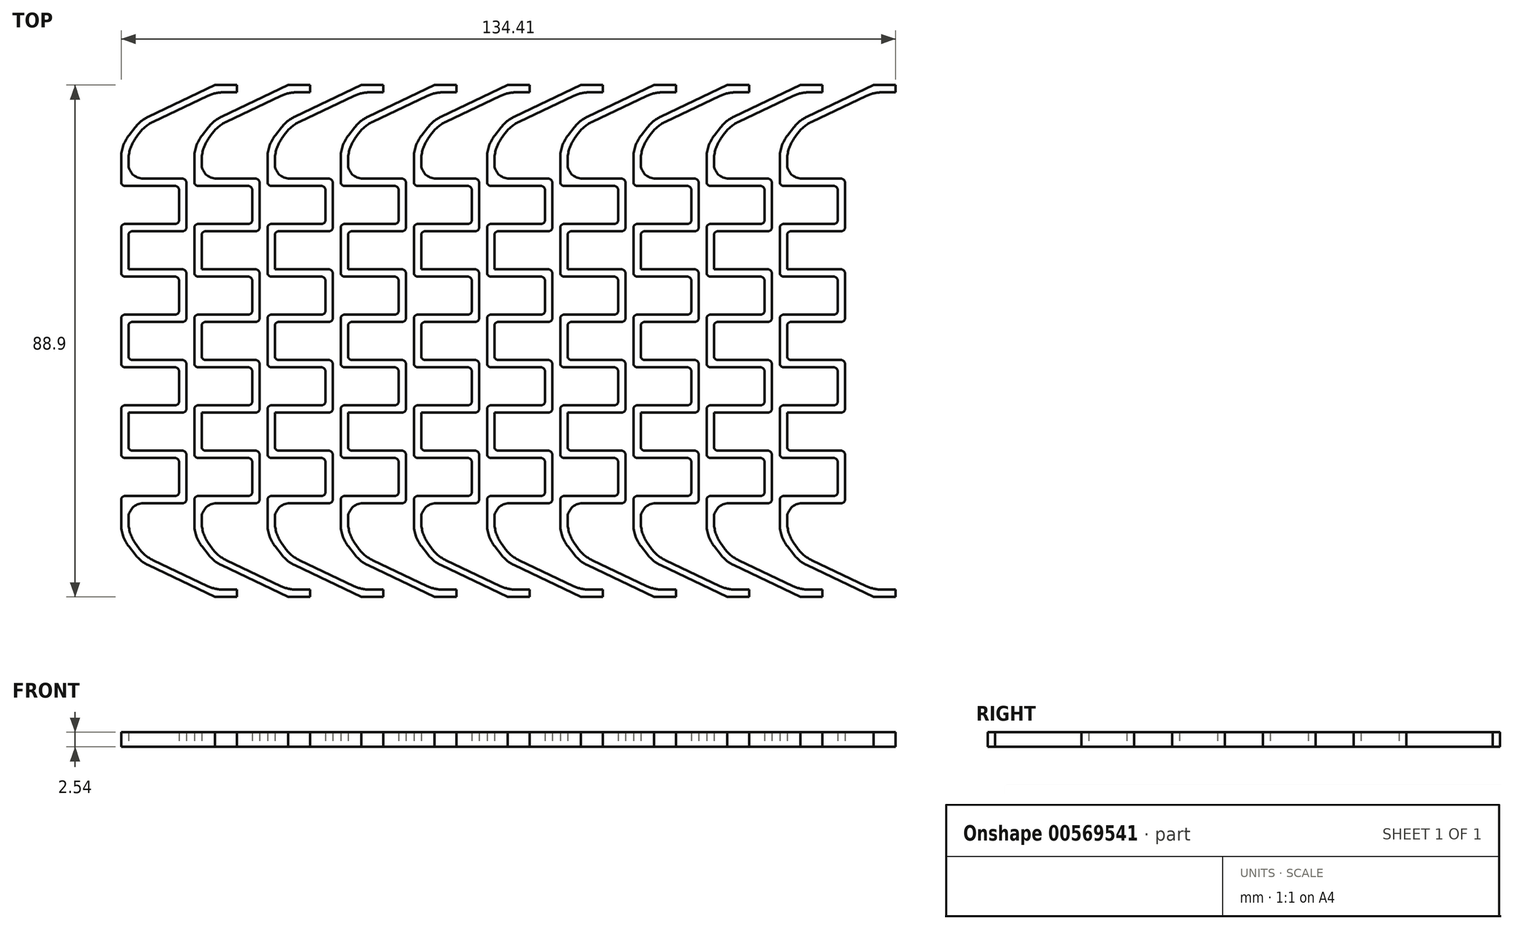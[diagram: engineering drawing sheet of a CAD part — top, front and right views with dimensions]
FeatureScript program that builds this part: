
annotation { "Feature Type Name" : "Feature", "Feature Type Description" : "" }
export const myFeature = defineFeature(function(context is Context, id is Id, definition is map)
    precondition{}
    {
        {
            var Q0;
            Q0=qCreatedBy(makeId("Top.planeOp"),FACE);
            var sketch = newSketch(context, id + "F0", { "sketchPlane" : qUnion([Q0])});
            skLineSegment(sketch, "E0", {"start": v(0, 44.45) * mm, "end": v(-11.59, 38.94) * mm});
            skLineSegment(sketch, "E1", {"start": v(0, 44.45) * mm, "end": v(3.81, 44.45) * mm});
            skLineSegment(sketch, "E2", {"start": v(3.81, 44.45) * mm, "end": v(3.81, 43.18) * mm});
            skLineSegment(sketch, "E3", {"start": v(3.81, 43.18) * mm, "end": v(1.43, 43.18) * mm});
            skPoint(sketch, "E4.visualSharp", {"position": v(0, 43.18) * mm});
            skLineSegment(sketch, "E5", {"start": v(-1.3, 42.56) * mm, "end": v(-10.77, 38.06) * mm});
            skLineSegment(sketch, "E6", {"start": v(-13.88, 37.1) * mm, "end": v(-14.96, 35.7) * mm});
            skLineSegment(sketch, "E7", {"start": v(-16.3, 31.8) * mm, "end": v(-16.3, 27.6) * mm});
            skLineSegment(sketch, "E8", {"start": v(-15.63, 26.92) * mm, "end": v(-6.93, 26.92) * mm});
            skLineSegment(sketch, "E9", {"start": v(-6.25, 26.25) * mm, "end": v(-6.25, 21) * mm});
            skLineSegment(sketch, "E10", {"start": v(-6.93, 20.32) * mm, "end": v(-15.63, 20.32) * mm});
            skLineSegment(sketch, "E11", {"start": v(-16.3, 19.65) * mm, "end": v(-16.3, 11.85) * mm});
            skLineSegment(sketch, "E12", {"start": v(-15.63, 11.18) * mm, "end": v(-6.93, 11.18) * mm});
            skLineSegment(sketch, "E13", {"start": v(-6.25, 10.5) * mm, "end": v(-6.25, 5.24) * mm});
            skLineSegment(sketch, "E14", {"start": v(-6.93, 4.57) * mm, "end": v(-15.63, 4.57) * mm});
            skLineSegment(sketch, "E15", {"start": v(-16.3, 3.9) * mm, "end": v(-16.3, 0) * mm});
            skLineSegment(sketch, "E16", {"start": v(-13.22, 36) * mm, "end": v(-13.85, 35.1) * mm});
            skLineSegment(sketch, "E17", {"start": v(-15.03, 31.43) * mm, "end": v(-15.03, 30.73) * mm});
            skLineSegment(sketch, "E18", {"start": v(-12.49, 28.2) * mm, "end": v(-5.66, 28.2) * mm});
            skLineSegment(sketch, "E19", {"start": v(-4.98, 27.52) * mm, "end": v(-4.98, 19.72) * mm});
            skLineSegment(sketch, "E20", {"start": v(-5.66, 19.05) * mm, "end": v(-14.36, 19.05) * mm});
            skLineSegment(sketch, "E21", {"start": v(-15.03, 18.38) * mm, "end": v(-15.03, 12.45) * mm});
            skLineSegment(sketch, "E22", {"start": v(-15.03, 12.45) * mm, "end": v(-5.66, 12.45) * mm});
            skLineSegment(sketch, "E23", {"start": v(-4.98, 11.77) * mm, "end": v(-4.98, 3.97) * mm});
            skLineSegment(sketch, "E24", {"start": v(-5.66, 3.3) * mm, "end": v(-14.36, 3.3) * mm});
            skLineSegment(sketch, "E25", {"start": v(-15.03, 2.63) * mm, "end": v(-15.03, 0) * mm});
            skArc(sketch, "E26.filletArc", {"start": v(1.43, 43.18) * mm, "mid": v(0.04, 43.02) * mm, "end": v(-1.3, 42.56) * mm});
            skPoint(sketch, "E27.visualSharp", {"position": v(-12.26, 37.35) * mm});
            skArc(sketch, "E27.filletArc", {"start": v(-10.77, 38.06) * mm, "mid": v(-12.13, 37.19) * mm, "end": v(-13.22, 36) * mm});
            skPoint(sketch, "E28.visualSharp", {"position": v(-15.03, 33.45) * mm});
            skArc(sketch, "E28.filletArc", {"start": v(-13.85, 35.1) * mm, "mid": v(-14.73, 33.36) * mm, "end": v(-15.03, 31.43) * mm});
            skPoint(sketch, "E29.visualSharp", {"position": v(-16.3, 33.98) * mm});
            skArc(sketch, "E29.filletArc", {"start": v(-14.96, 35.7) * mm, "mid": v(-15.96, 33.86) * mm, "end": v(-16.3, 31.8) * mm});
            skPoint(sketch, "E30.visualSharp", {"position": v(-12.95, 38.29) * mm});
            skArc(sketch, "E30.filletArc", {"start": v(-11.59, 38.94) * mm, "mid": v(-12.84, 38.15) * mm, "end": v(-13.88, 37.1) * mm});
            skPoint(sketch, "E31.visualSharp", {"position": v(-15.03, 28.2) * mm});
            skArc(sketch, "E31.filletArc", {"start": v(-15.03, 30.73) * mm, "mid": v(-14.29, 28.94) * mm, "end": v(-12.49, 28.2) * mm});
            skPoint(sketch, "E32.visualSharp", {"position": v(-16.3, 26.92) * mm});
            skArc(sketch, "E32.filletArc", {"start": v(-16.3, 27.6) * mm, "mid": v(-16.1, 27.12) * mm, "end": v(-15.63, 26.92) * mm});
            skPoint(sketch, "E33.visualSharp", {"position": v(-6.25, 26.92) * mm});
            skArc(sketch, "E33.filletArc", {"start": v(-6.25, 26.25) * mm, "mid": v(-6.45, 26.73) * mm, "end": v(-6.93, 26.92) * mm});
            skPoint(sketch, "E34.visualSharp", {"position": v(-4.98, 28.2) * mm});
            skArc(sketch, "E34.filletArc", {"start": v(-4.98, 27.52) * mm, "mid": v(-5.18, 28) * mm, "end": v(-5.66, 28.2) * mm});
            skPoint(sketch, "E35.visualSharp", {"position": v(-6.25, 20.32) * mm});
            skArc(sketch, "E35.filletArc", {"start": v(-6.93, 20.32) * mm, "mid": v(-6.45, 20.52) * mm, "end": v(-6.25, 21) * mm});
            skPoint(sketch, "E36.visualSharp", {"position": v(-4.98, 19.05) * mm});
            skArc(sketch, "E36.filletArc", {"start": v(-5.66, 19.05) * mm, "mid": v(-5.18, 19.25) * mm, "end": v(-4.98, 19.72) * mm});
            skPoint(sketch, "E37.visualSharp", {"position": v(-16.3, 20.32) * mm});
            skArc(sketch, "E37.filletArc", {"start": v(-15.63, 20.32) * mm, "mid": v(-16.1, 20.12) * mm, "end": v(-16.3, 19.65) * mm});
            skPoint(sketch, "E38.visualSharp", {"position": v(-16.3, 11.18) * mm});
            skArc(sketch, "E38.filletArc", {"start": v(-16.3, 11.85) * mm, "mid": v(-16.1, 11.37) * mm, "end": v(-15.63, 11.18) * mm});
            skPoint(sketch, "E39.visualSharp", {"position": v(-15.03, 19.05) * mm});
            skArc(sketch, "E39.filletArc", {"start": v(-14.36, 19.05) * mm, "mid": v(-14.83, 18.85) * mm, "end": v(-15.03, 18.38) * mm});
            skPoint(sketch, "E40.visualSharp", {"position": v(-4.98, 12.45) * mm});
            skArc(sketch, "E40.filletArc", {"start": v(-4.98, 11.77) * mm, "mid": v(-5.18, 12.25) * mm, "end": v(-5.66, 12.45) * mm});
            skPoint(sketch, "E41.visualSharp", {"position": v(-6.25, 11.18) * mm});
            skArc(sketch, "E41.filletArc", {"start": v(-6.25, 10.5) * mm, "mid": v(-6.45, 10.98) * mm, "end": v(-6.93, 11.18) * mm});
            skPoint(sketch, "E42.visualSharp", {"position": v(-4.98, 3.3) * mm});
            skArc(sketch, "E42.filletArc", {"start": v(-5.66, 3.3) * mm, "mid": v(-5.18, 3.5) * mm, "end": v(-4.98, 3.97) * mm});
            skPoint(sketch, "E43.visualSharp", {"position": v(-15.03, 3.3) * mm});
            skArc(sketch, "E43.filletArc", {"start": v(-14.36, 3.3) * mm, "mid": v(-14.83, 3.1) * mm, "end": v(-15.03, 2.63) * mm});
            skPoint(sketch, "E44.visualSharp", {"position": v(-6.25, 4.57) * mm});
            skArc(sketch, "E44.filletArc", {"start": v(-6.93, 4.57) * mm, "mid": v(-6.45, 4.77) * mm, "end": v(-6.25, 5.24) * mm});
            skPoint(sketch, "E45.visualSharp", {"position": v(-16.3, 4.57) * mm});
            skArc(sketch, "E45.filletArc", {"start": v(-15.63, 4.57) * mm, "mid": v(-16.1, 4.38) * mm, "end": v(-16.3, 3.9) * mm});
            skArc(sketch, "E46.MirrorCS", {"start": v(-15.03, -30.73) * mm, "mid": v(-14.29, -28.94) * mm, "end": v(-12.49, -28.2) * mm});
            skArc(sketch, "E47.MirrorCS", {"start": v(-15.63, -4.57) * mm, "mid": v(-16.1, -4.38) * mm, "end": v(-16.3, -3.9) * mm});
            skArc(sketch, "E48.MirrorCS", {"start": v(-14.36, -19.05) * mm, "mid": v(-14.83, -18.85) * mm, "end": v(-15.03, -18.38) * mm});
            skArc(sketch, "E49.MirrorCS", {"start": v(-14.36, -3.3) * mm, "mid": v(-14.83, -3.1) * mm, "end": v(-15.03, -2.63) * mm});
            skArc(sketch, "E50.MirrorCS", {"start": v(-6.25, -26.25) * mm, "mid": v(-6.45, -26.73) * mm, "end": v(-6.93, -26.92) * mm});
            skArc(sketch, "E51.MirrorCS", {"start": v(-4.98, -27.52) * mm, "mid": v(-5.18, -28) * mm, "end": v(-5.66, -28.2) * mm});
            skArc(sketch, "E52.MirrorCS", {"start": v(-15.63, -20.32) * mm, "mid": v(-16.1, -20.12) * mm, "end": v(-16.3, -19.65) * mm});
            skArc(sketch, "E53.MirrorCS", {"start": v(-6.25, -10.5) * mm, "mid": v(-6.45, -10.98) * mm, "end": v(-6.93, -11.18) * mm});
            skArc(sketch, "E54.MirrorCS", {"start": v(-6.93, -20.32) * mm, "mid": v(-6.45, -20.52) * mm, "end": v(-6.25, -21) * mm});
            skArc(sketch, "E55.MirrorCS", {"start": v(-5.66, -19.05) * mm, "mid": v(-5.18, -19.25) * mm, "end": v(-4.98, -19.72) * mm});
            skArc(sketch, "E56.MirrorCS", {"start": v(-16.3, -11.85) * mm, "mid": v(-16.1, -11.37) * mm, "end": v(-15.63, -11.18) * mm});
            skArc(sketch, "E57.MirrorCS", {"start": v(-4.98, -11.77) * mm, "mid": v(-5.18, -12.25) * mm, "end": v(-5.66, -12.45) * mm});
            skLineSegment(sketch, "E58.MirrorCS", {"start": v(-13.22, -36) * mm, "end": v(-13.85, -35.1) * mm});
            skArc(sketch, "E59.MirrorCS", {"start": v(-6.93, -4.57) * mm, "mid": v(-6.45, -4.77) * mm, "end": v(-6.25, -5.24) * mm});
            skArc(sketch, "E60.MirrorCS", {"start": v(-5.66, -3.3) * mm, "mid": v(-5.18, -3.5) * mm, "end": v(-4.98, -3.97) * mm});
            skArc(sketch, "E61.MirrorCS", {"start": v(-16.3, -27.6) * mm, "mid": v(-16.1, -27.12) * mm, "end": v(-15.63, -26.92) * mm});
            skArc(sketch, "E62.MirrorCS", {"start": v(-11.59, -38.94) * mm, "mid": v(-12.84, -38.15) * mm, "end": v(-13.88, -37.1) * mm});
            skLineSegment(sketch, "E63.MirrorCS", {"start": v(-15.03, -31.43) * mm, "end": v(-15.03, -30.73) * mm});
            skLineSegment(sketch, "E64.MirrorCS", {"start": v(-13.88, -37.1) * mm, "end": v(-14.96, -35.7) * mm});
            skLineSegment(sketch, "E65.MirrorCS", {"start": v(-16.3, -31.8) * mm, "end": v(-16.3, -27.6) * mm});
            skArc(sketch, "E66.MirrorCS", {"start": v(-10.77, -38.06) * mm, "mid": v(-12.13, -37.19) * mm, "end": v(-13.22, -36) * mm});
            skPoint(sketch, "E67.MirrorP", {"position": v(-15.03, -19.05) * mm});
            skLineSegment(sketch, "E68.MirrorCS", {"start": v(-15.03, -2.63) * mm, "end": v(-15.03, 0) * mm});
            skPoint(sketch, "E69.MirrorP", {"position": v(-15.03, -28.2) * mm});
            skArc(sketch, "E70.MirrorCS", {"start": v(-14.96, -35.7) * mm, "mid": v(-15.96, -33.86) * mm, "end": v(-16.3, -31.8) * mm});
            skArc(sketch, "E71.MirrorCS", {"start": v(-13.85, -35.1) * mm, "mid": v(-14.73, -33.36) * mm, "end": v(-15.03, -31.43) * mm});
            skPoint(sketch, "E72.MirrorP", {"position": v(-15.03, -3.3) * mm});
            skLineSegment(sketch, "E73.MirrorCS", {"start": v(-16.3, -3.9) * mm, "end": v(-16.3, 0) * mm});
            skLineSegment(sketch, "E74.MirrorCS", {"start": v(-16.3, -19.65) * mm, "end": v(-16.3, -11.85) * mm});
            skLineSegment(sketch, "E75.MirrorCS", {"start": v(-12.49, -28.2) * mm, "end": v(-5.66, -28.2) * mm});
            skPoint(sketch, "E76.MirrorP", {"position": v(-16.3, -26.92) * mm});
            skPoint(sketch, "E77.MirrorP", {"position": v(-16.3, -11.18) * mm});
            skPoint(sketch, "E78.MirrorP", {"position": v(-6.25, -20.32) * mm});
            skPoint(sketch, "E79.MirrorP", {"position": v(-4.98, -12.45) * mm});
            skLineSegment(sketch, "E80.MirrorCS", {"start": v(-15.63, -26.92) * mm, "end": v(-6.93, -26.92) * mm});
            skLineSegment(sketch, "E81.MirrorCS", {"start": v(-15.03, -18.38) * mm, "end": v(-15.03, -12.45) * mm});
            skPoint(sketch, "E82.MirrorP", {"position": v(-6.25, -11.18) * mm});
            skLineSegment(sketch, "E83.MirrorCS", {"start": v(-15.03, -12.45) * mm, "end": v(-5.66, -12.45) * mm});
            skLineSegment(sketch, "E84.MirrorCS", {"start": v(-5.66, -3.3) * mm, "end": v(-14.36, -3.3) * mm});
            skPoint(sketch, "E85.MirrorP", {"position": v(-15.03, -33.45) * mm});
            skPoint(sketch, "E86.MirrorP", {"position": v(-4.98, -3.3) * mm});
            skLineSegment(sketch, "E87.MirrorCS", {"start": v(-15.63, -11.18) * mm, "end": v(-6.93, -11.18) * mm});
            skLineSegment(sketch, "E88.MirrorCS", {"start": v(-6.25, -10.5) * mm, "end": v(-6.25, -5.24) * mm});
            skLineSegment(sketch, "E89.MirrorCS", {"start": v(-6.25, -26.25) * mm, "end": v(-6.25, -21) * mm});
            skPoint(sketch, "E90.MirrorP", {"position": v(-16.3, -33.98) * mm});
            skPoint(sketch, "E91.MirrorP", {"position": v(-16.3, -20.32) * mm});
            skPoint(sketch, "E92.MirrorP", {"position": v(-16.3, -4.57) * mm});
            skLineSegment(sketch, "E93.MirrorCS", {"start": v(-6.93, -4.57) * mm, "end": v(-15.63, -4.57) * mm});
            skPoint(sketch, "E94.MirrorP", {"position": v(-12.26, -37.35) * mm});
            skPoint(sketch, "E95.MirrorP", {"position": v(-4.98, -19.05) * mm});
            skPoint(sketch, "E96.MirrorP", {"position": v(-6.25, -4.57) * mm});
            skPoint(sketch, "E97.MirrorP", {"position": v(-4.98, -28.2) * mm});
            skLineSegment(sketch, "E98.MirrorCS", {"start": v(-5.66, -19.05) * mm, "end": v(-14.36, -19.05) * mm});
            skLineSegment(sketch, "E99.MirrorCS", {"start": v(-4.98, -11.77) * mm, "end": v(-4.98, -3.97) * mm});
            skPoint(sketch, "E100.MirrorP", {"position": v(-12.95, -38.29) * mm});
            skPoint(sketch, "E101.MirrorP", {"position": v(-6.25, -26.92) * mm});
            skLineSegment(sketch, "E102.MirrorCS", {"start": v(-4.98, -27.52) * mm, "end": v(-4.98, -19.72) * mm});
            skLineSegment(sketch, "E103.MirrorCS", {"start": v(-6.93, -20.32) * mm, "end": v(-15.63, -20.32) * mm});
            skLineSegment(sketch, "E104.MirrorCS", {"start": v(3.81, -44.45) * mm, "end": v(3.81, -43.18) * mm});
            skArc(sketch, "E105.MirrorCS", {"start": v(1.43, -43.18) * mm, "mid": v(0.04, -43.02) * mm, "end": v(-1.3, -42.56) * mm});
            skPoint(sketch, "E106.MirrorP", {"position": v(0, -43.18) * mm});
            skLineSegment(sketch, "E107.MirrorCS", {"start": v(3.81, -43.18) * mm, "end": v(1.43, -43.18) * mm});
            skLineSegment(sketch, "E108.MirrorCS", {"start": v(0, -44.45) * mm, "end": v(3.81, -44.45) * mm});
            skLineSegment(sketch, "E109.MirrorCS", {"start": v(-1.3, -42.56) * mm, "end": v(-10.77, -38.06) * mm});
            skLineSegment(sketch, "E110.MirrorCS", {"start": v(0, -44.45) * mm, "end": v(-11.59, -38.94) * mm});
            skPoint(sketch, "E111.1.0.0", {"position": v(-2.33, 33.45) * mm});
            skPoint(sketch, "E111.1.0.1", {"position": v(7.72, 19.05) * mm});
            skPoint(sketch, "E111.1.0.2", {"position": v(-3.6, -26.92) * mm});
            skLineSegment(sketch, "E111.1.0.3", {"start": v(-2.33, -12.45) * mm, "end": v(7.04, -12.45) * mm});
            skLineSegment(sketch, "E111.1.0.4", {"start": v(5.77, -20.32) * mm, "end": v(-2.93, -20.32) * mm});
            skPoint(sketch, "E111.1.0.5", {"position": v(-3.6, -33.98) * mm});
            skPoint(sketch, "E111.1.0.6", {"position": v(-0.25, 38.29) * mm});
            skPoint(sketch, "E111.1.0.7", {"position": v(0.44, -37.35) * mm});
            skPoint(sketch, "E111.1.0.8", {"position": v(-3.6, -11.18) * mm});
            skLineSegment(sketch, "E111.1.0.9", {"start": v(7.04, -3.3) * mm, "end": v(-1.66, -3.3) * mm});
            skPoint(sketch, "E111.1.0.10", {"position": v(-3.6, 20.32) * mm});
            skPoint(sketch, "E111.1.0.11", {"position": v(-3.6, -20.32) * mm});
            skPoint(sketch, "E111.1.0.12", {"position": v(-3.6, 33.98) * mm});
            skPoint(sketch, "E111.1.0.13", {"position": v(7.72, -3.3) * mm});
            skPoint(sketch, "E111.1.0.14", {"position": v(6.45, -11.18) * mm});
            skPoint(sketch, "E111.1.0.15", {"position": v(7.72, -12.45) * mm});
            skLineSegment(sketch, "E111.1.0.16", {"start": v(5.77, -4.57) * mm, "end": v(-2.93, -4.57) * mm});
            skPoint(sketch, "E111.1.0.17", {"position": v(12.7, -43.18) * mm});
            skPoint(sketch, "E111.1.0.18", {"position": v(7.72, -19.05) * mm});
            skPoint(sketch, "E111.1.0.19", {"position": v(12.7, 43.18) * mm});
            skPoint(sketch, "E111.1.0.20", {"position": v(7.72, -28.2) * mm});
            skPoint(sketch, "E111.1.0.21", {"position": v(-3.6, 26.92) * mm});
            skPoint(sketch, "E111.1.0.22", {"position": v(0.44, 37.35) * mm});
            skPoint(sketch, "E111.1.0.23", {"position": v(-2.33, -33.45) * mm});
            skLineSegment(sketch, "E111.1.0.24", {"start": v(12.7, 44.45) * mm, "end": v(1.11, 38.94) * mm});
            skPoint(sketch, "E111.1.0.25", {"position": v(6.45, -20.32) * mm});
            skPoint(sketch, "E111.1.0.26", {"position": v(-2.33, -3.3) * mm});
            skPoint(sketch, "E111.1.0.27", {"position": v(6.45, -26.92) * mm});
            skLineSegment(sketch, "E111.1.0.28", {"start": v(7.04, -19.05) * mm, "end": v(-1.66, -19.05) * mm});
            skLineSegment(sketch, "E111.1.0.29", {"start": v(11.4, -42.56) * mm, "end": v(1.93, -38.06) * mm});
            skPoint(sketch, "E111.1.0.30", {"position": v(-3.6, -4.57) * mm});
            skPoint(sketch, "E111.1.0.31", {"position": v(-2.33, -28.2) * mm});
            skLineSegment(sketch, "E111.1.0.32", {"start": v(12.7, -44.45) * mm, "end": v(1.11, -38.94) * mm});
            skLineSegment(sketch, "E111.1.0.33", {"start": v(11.4, 42.56) * mm, "end": v(1.93, 38.06) * mm});
            skPoint(sketch, "E111.1.0.34", {"position": v(6.45, -4.57) * mm});
            skPoint(sketch, "E111.1.0.35", {"position": v(-0.25, -38.29) * mm});
            skLineSegment(sketch, "E111.1.0.36", {"start": v(-2.93, -11.18) * mm, "end": v(5.77, -11.18) * mm});
            skPoint(sketch, "E111.1.0.37", {"position": v(-2.33, -19.05) * mm});
            skPoint(sketch, "E111.1.0.38", {"position": v(6.45, 4.57) * mm});
            skPoint(sketch, "E111.1.0.39", {"position": v(6.45, 26.92) * mm});
            skPoint(sketch, "E111.1.0.40", {"position": v(6.45, 11.18) * mm});
            skLineSegment(sketch, "E111.1.0.41", {"start": v(7.04, 19.05) * mm, "end": v(-1.66, 19.05) * mm});
            skPoint(sketch, "E111.1.0.42", {"position": v(12.7, 43.18) * mm});
            skPoint(sketch, "E111.1.0.43", {"position": v(12.7, -43.18) * mm});
            skPoint(sketch, "E111.1.0.44", {"position": v(-3.6, 11.18) * mm});
            skPoint(sketch, "E111.1.0.45", {"position": v(-3.6, 4.57) * mm});
            skLineSegment(sketch, "E111.1.0.46", {"start": v(7.04, 3.3) * mm, "end": v(-1.66, 3.3) * mm});
            skLineSegment(sketch, "E111.1.0.47", {"start": v(5.77, 4.57) * mm, "end": v(-2.93, 4.57) * mm});
            skPoint(sketch, "E111.1.0.48", {"position": v(6.45, 20.32) * mm});
            skPoint(sketch, "E111.1.0.49", {"position": v(-2.33, 19.05) * mm});
            skPoint(sketch, "E111.1.0.50", {"position": v(-2.33, 28.2) * mm});
            skPoint(sketch, "E111.1.0.51", {"position": v(-2.33, 3.3) * mm});
            skLineSegment(sketch, "E111.1.0.52", {"start": v(5.77, 20.32) * mm, "end": v(-2.93, 20.32) * mm});
            skLineSegment(sketch, "E111.1.0.53", {"start": v(-2.33, 12.45) * mm, "end": v(7.04, 12.45) * mm});
            skPoint(sketch, "E111.1.0.54", {"position": v(7.72, 28.2) * mm});
            skLineSegment(sketch, "E111.1.0.55", {"start": v(-2.93, 11.18) * mm, "end": v(5.77, 11.18) * mm});
            skPoint(sketch, "E111.1.0.56", {"position": v(7.72, 12.45) * mm});
            skPoint(sketch, "E111.1.0.57", {"position": v(7.72, 3.3) * mm});
            skLineSegment(sketch, "E111.1.0.58", {"start": v(16.51, -43.18) * mm, "end": v(14.13, -43.18) * mm});
            skLineSegment(sketch, "E111.1.0.59", {"start": v(12.7, -44.45) * mm, "end": v(16.51, -44.45) * mm});
            skLineSegment(sketch, "E111.1.0.60", {"start": v(-2.93, -26.92) * mm, "end": v(5.77, -26.92) * mm});
            skLineSegment(sketch, "E111.1.0.61", {"start": v(16.51, 43.18) * mm, "end": v(14.13, 43.18) * mm});
            skLineSegment(sketch, "E111.1.0.62", {"start": v(16.51, 44.45) * mm, "end": v(16.51, 43.18) * mm});
            skLineSegment(sketch, "E111.1.0.63", {"start": v(7.72, -27.52) * mm, "end": v(7.72, -19.72) * mm});
            skArc(sketch, "E111.1.0.64", {"start": v(1.93, 38.06) * mm, "mid": v(0.57, 37.19) * mm, "end": v(-0.52, 36) * mm});
            skLineSegment(sketch, "E111.1.0.65", {"start": v(16.51, -44.45) * mm, "end": v(16.51, -43.18) * mm});
            skLineSegment(sketch, "E111.1.0.66", {"start": v(6.45, -10.5) * mm, "end": v(6.45, -5.24) * mm});
            skArc(sketch, "E111.1.0.67", {"start": v(1.11, -38.94) * mm, "mid": v(-0.14, -38.15) * mm, "end": v(-1.18, -37.1) * mm});
            skLineSegment(sketch, "E111.1.0.68", {"start": v(-3.6, -19.65) * mm, "end": v(-3.6, -11.85) * mm});
            skLineSegment(sketch, "E111.1.0.69", {"start": v(0.21, -28.2) * mm, "end": v(7.04, -28.2) * mm});
            skLineSegment(sketch, "E111.1.0.70", {"start": v(6.45, -26.25) * mm, "end": v(6.45, -21) * mm});
            skLineSegment(sketch, "E111.1.0.71", {"start": v(0.21, 28.2) * mm, "end": v(7.04, 28.2) * mm});
            skLineSegment(sketch, "E111.1.0.72", {"start": v(7.72, -11.77) * mm, "end": v(7.72, -3.97) * mm});
            skLineSegment(sketch, "E111.1.0.73", {"start": v(12.7, 44.45) * mm, "end": v(16.51, 44.45) * mm});
            skLineSegment(sketch, "E111.1.0.74", {"start": v(-2.33, -18.38) * mm, "end": v(-2.33, -12.45) * mm});
            skArc(sketch, "E111.1.0.75", {"start": v(1.93, -38.06) * mm, "mid": v(0.57, -37.19) * mm, "end": v(-0.52, -36) * mm});
            skLineSegment(sketch, "E111.1.0.76", {"start": v(-2.93, 26.92) * mm, "end": v(5.77, 26.92) * mm});
            skArc(sketch, "E111.1.0.77", {"start": v(-2.26, 35.7) * mm, "mid": v(-3.26, 33.86) * mm, "end": v(-3.6, 31.8) * mm});
            skArc(sketch, "E111.1.0.78", {"start": v(7.72, -27.52) * mm, "mid": v(7.52, -28) * mm, "end": v(7.04, -28.2) * mm});
            skLineSegment(sketch, "E111.1.0.79", {"start": v(7.72, 27.52) * mm, "end": v(7.72, 19.72) * mm});
            skArc(sketch, "E111.1.0.80", {"start": v(5.77, -4.57) * mm, "mid": v(6.25, -4.77) * mm, "end": v(6.45, -5.24) * mm});
            skArc(sketch, "E111.1.0.81", {"start": v(-2.26, -35.7) * mm, "mid": v(-3.26, -33.86) * mm, "end": v(-3.6, -31.8) * mm});
            skArc(sketch, "E111.1.0.82", {"start": v(-2.93, -20.32) * mm, "mid": v(-3.4, -20.12) * mm, "end": v(-3.6, -19.65) * mm});
            skArc(sketch, "E111.1.0.83", {"start": v(7.04, -3.3) * mm, "mid": v(7.52, -3.5) * mm, "end": v(7.72, -3.97) * mm});
            skArc(sketch, "E111.1.0.84", {"start": v(-1.15, 35.1) * mm, "mid": v(-2.03, 33.36) * mm, "end": v(-2.33, 31.43) * mm});
            skLineSegment(sketch, "E111.1.0.85", {"start": v(-2.33, 18.38) * mm, "end": v(-2.33, 12.45) * mm});
            skArc(sketch, "E111.1.0.86", {"start": v(-1.15, -35.1) * mm, "mid": v(-2.03, -33.36) * mm, "end": v(-2.33, -31.43) * mm});
            skArc(sketch, "E111.1.0.87", {"start": v(-2.33, -30.73) * mm, "mid": v(-1.59, -28.94) * mm, "end": v(0.21, -28.2) * mm});
            skArc(sketch, "E111.1.0.88", {"start": v(6.45, -10.5) * mm, "mid": v(6.25, -10.98) * mm, "end": v(5.77, -11.18) * mm});
            skArc(sketch, "E111.1.0.89", {"start": v(-2.93, 20.32) * mm, "mid": v(-3.4, 20.12) * mm, "end": v(-3.6, 19.65) * mm});
            skArc(sketch, "E111.1.0.90", {"start": v(1.11, 38.94) * mm, "mid": v(-0.14, 38.15) * mm, "end": v(-1.18, 37.1) * mm});
            skLineSegment(sketch, "E111.1.0.91", {"start": v(6.45, 10.5) * mm, "end": v(6.45, 5.24) * mm});
            skArc(sketch, "E111.1.0.92", {"start": v(-2.33, 30.73) * mm, "mid": v(-1.59, 28.94) * mm, "end": v(0.21, 28.2) * mm});
            skArc(sketch, "E111.1.0.93", {"start": v(14.13, 43.18) * mm, "mid": v(12.74, 43.02) * mm, "end": v(11.4, 42.56) * mm});
            skLineSegment(sketch, "E111.1.0.94", {"start": v(-0.52, -36) * mm, "end": v(-1.15, -35.1) * mm});
            skArc(sketch, "E111.1.0.95", {"start": v(-1.66, -19.05) * mm, "mid": v(-2.13, -18.85) * mm, "end": v(-2.33, -18.38) * mm});
            skArc(sketch, "E111.1.0.96", {"start": v(-1.66, 19.05) * mm, "mid": v(-2.13, 18.85) * mm, "end": v(-2.33, 18.38) * mm});
            skLineSegment(sketch, "E111.1.0.97", {"start": v(-3.6, -31.8) * mm, "end": v(-3.6, -27.6) * mm});
            skArc(sketch, "E111.1.0.98", {"start": v(7.72, -11.77) * mm, "mid": v(7.52, -12.25) * mm, "end": v(7.04, -12.45) * mm});
            skLineSegment(sketch, "E111.1.0.99", {"start": v(7.72, 11.77) * mm, "end": v(7.72, 3.97) * mm});
            skLineSegment(sketch, "E111.1.0.100", {"start": v(-2.33, 31.43) * mm, "end": v(-2.33, 30.73) * mm});
            skLineSegment(sketch, "E111.1.0.101", {"start": v(6.45, 26.25) * mm, "end": v(6.45, 21) * mm});
            skArc(sketch, "E111.1.0.102", {"start": v(5.77, -20.32) * mm, "mid": v(6.25, -20.52) * mm, "end": v(6.45, -21) * mm});
            skArc(sketch, "E111.1.0.103", {"start": v(-3.6, -11.85) * mm, "mid": v(-3.4, -11.37) * mm, "end": v(-2.93, -11.18) * mm});
            skLineSegment(sketch, "E111.1.0.104", {"start": v(-1.18, 37.1) * mm, "end": v(-2.26, 35.7) * mm});
            skLineSegment(sketch, "E111.1.0.105", {"start": v(-3.6, 31.8) * mm, "end": v(-3.6, 27.6) * mm});
            skArc(sketch, "E111.1.0.106", {"start": v(14.13, -43.18) * mm, "mid": v(12.74, -43.02) * mm, "end": v(11.4, -42.56) * mm});
            skArc(sketch, "E111.1.0.107", {"start": v(7.04, -19.05) * mm, "mid": v(7.52, -19.25) * mm, "end": v(7.72, -19.72) * mm});
            skLineSegment(sketch, "E111.1.0.108", {"start": v(-1.18, -37.1) * mm, "end": v(-2.26, -35.7) * mm});
            skLineSegment(sketch, "E111.1.0.109", {"start": v(-0.52, 36) * mm, "end": v(-1.15, 35.1) * mm});
            skLineSegment(sketch, "E111.1.0.110", {"start": v(-3.6, 19.65) * mm, "end": v(-3.6, 11.85) * mm});
            skArc(sketch, "E111.1.0.111", {"start": v(6.45, -26.25) * mm, "mid": v(6.25, -26.73) * mm, "end": v(5.77, -26.92) * mm});
            skArc(sketch, "E111.1.0.112", {"start": v(-3.6, -27.6) * mm, "mid": v(-3.4, -27.12) * mm, "end": v(-2.93, -26.92) * mm});
            skArc(sketch, "E111.1.0.113", {"start": v(5.77, 20.32) * mm, "mid": v(6.25, 20.52) * mm, "end": v(6.45, 21) * mm});
            skLineSegment(sketch, "E111.1.0.114", {"start": v(-2.33, -2.63) * mm, "end": v(-2.33, 0) * mm});
            skArc(sketch, "E111.1.0.115", {"start": v(-1.66, 3.3) * mm, "mid": v(-2.13, 3.1) * mm, "end": v(-2.33, 2.63) * mm});
            skArc(sketch, "E111.1.0.116", {"start": v(7.04, 19.05) * mm, "mid": v(7.52, 19.25) * mm, "end": v(7.72, 19.72) * mm});
            skArc(sketch, "E111.1.0.117", {"start": v(5.77, 4.57) * mm, "mid": v(6.25, 4.77) * mm, "end": v(6.45, 5.24) * mm});
            skArc(sketch, "E111.1.0.118", {"start": v(7.04, 3.3) * mm, "mid": v(7.52, 3.5) * mm, "end": v(7.72, 3.97) * mm});
            skArc(sketch, "E111.1.0.119", {"start": v(7.72, 11.77) * mm, "mid": v(7.52, 12.25) * mm, "end": v(7.04, 12.45) * mm});
            skLineSegment(sketch, "E111.1.0.120", {"start": v(-2.33, -31.43) * mm, "end": v(-2.33, -30.73) * mm});
            skLineSegment(sketch, "E111.1.0.121", {"start": v(-3.6, -3.9) * mm, "end": v(-3.6, 0) * mm});
            skArc(sketch, "E111.1.0.122", {"start": v(7.72, 27.52) * mm, "mid": v(7.52, 28) * mm, "end": v(7.04, 28.2) * mm});
            skArc(sketch, "E111.1.0.123", {"start": v(6.45, 26.25) * mm, "mid": v(6.25, 26.73) * mm, "end": v(5.77, 26.92) * mm});
            skArc(sketch, "E111.1.0.124", {"start": v(-2.93, -4.57) * mm, "mid": v(-3.4, -4.38) * mm, "end": v(-3.6, -3.9) * mm});
            skArc(sketch, "E111.1.0.125", {"start": v(-1.66, -3.3) * mm, "mid": v(-2.13, -3.1) * mm, "end": v(-2.33, -2.63) * mm});
            skArc(sketch, "E111.1.0.126", {"start": v(-3.6, 11.85) * mm, "mid": v(-3.4, 11.37) * mm, "end": v(-2.93, 11.18) * mm});
            skArc(sketch, "E111.1.0.127", {"start": v(-2.93, 4.57) * mm, "mid": v(-3.4, 4.38) * mm, "end": v(-3.6, 3.9) * mm});
            skArc(sketch, "E111.1.0.128", {"start": v(-3.6, 27.6) * mm, "mid": v(-3.4, 27.12) * mm, "end": v(-2.93, 26.92) * mm});
            skLineSegment(sketch, "E111.1.0.129", {"start": v(-2.33, 2.63) * mm, "end": v(-2.33, 0) * mm});
            skArc(sketch, "E111.1.0.130", {"start": v(6.45, 10.5) * mm, "mid": v(6.25, 10.98) * mm, "end": v(5.77, 11.18) * mm});
            skLineSegment(sketch, "E111.1.0.131", {"start": v(-3.6, 3.9) * mm, "end": v(-3.6, 0) * mm});
            skPoint(sketch, "E111.2.0.0", {"position": v(10.37, 33.45) * mm});
            skPoint(sketch, "E111.2.0.1", {"position": v(20.42, 19.05) * mm});
            skPoint(sketch, "E111.2.0.2", {"position": v(9.1, -26.92) * mm});
            skLineSegment(sketch, "E111.2.0.3", {"start": v(10.37, -12.45) * mm, "end": v(19.74, -12.45) * mm});
            skLineSegment(sketch, "E111.2.0.4", {"start": v(18.47, -20.32) * mm, "end": v(9.77, -20.32) * mm});
            skPoint(sketch, "E111.2.0.5", {"position": v(9.1, -33.98) * mm});
            skPoint(sketch, "E111.2.0.6", {"position": v(12.45, 38.29) * mm});
            skPoint(sketch, "E111.2.0.7", {"position": v(13.14, -37.35) * mm});
            skPoint(sketch, "E111.2.0.8", {"position": v(9.1, -11.18) * mm});
            skLineSegment(sketch, "E111.2.0.9", {"start": v(19.74, -3.3) * mm, "end": v(11.04, -3.3) * mm});
            skPoint(sketch, "E111.2.0.10", {"position": v(9.1, 20.32) * mm});
            skPoint(sketch, "E111.2.0.11", {"position": v(9.1, -20.32) * mm});
            skPoint(sketch, "E111.2.0.12", {"position": v(9.1, 33.98) * mm});
            skPoint(sketch, "E111.2.0.13", {"position": v(20.42, -3.3) * mm});
            skPoint(sketch, "E111.2.0.14", {"position": v(19.15, -11.18) * mm});
            skPoint(sketch, "E111.2.0.15", {"position": v(20.42, -12.45) * mm});
            skLineSegment(sketch, "E111.2.0.16", {"start": v(18.47, -4.57) * mm, "end": v(9.77, -4.57) * mm});
            skPoint(sketch, "E111.2.0.17", {"position": v(25.4, -43.18) * mm});
            skPoint(sketch, "E111.2.0.18", {"position": v(20.42, -19.05) * mm});
            skPoint(sketch, "E111.2.0.19", {"position": v(25.4, 43.18) * mm});
            skPoint(sketch, "E111.2.0.20", {"position": v(20.42, -28.2) * mm});
            skPoint(sketch, "E111.2.0.21", {"position": v(9.1, 26.92) * mm});
            skPoint(sketch, "E111.2.0.22", {"position": v(13.14, 37.35) * mm});
            skPoint(sketch, "E111.2.0.23", {"position": v(10.37, -33.45) * mm});
            skLineSegment(sketch, "E111.2.0.24", {"start": v(25.4, 44.45) * mm, "end": v(13.81, 38.94) * mm});
            skPoint(sketch, "E111.2.0.25", {"position": v(19.15, -20.32) * mm});
            skPoint(sketch, "E111.2.0.26", {"position": v(10.37, -3.3) * mm});
            skPoint(sketch, "E111.2.0.27", {"position": v(19.15, -26.92) * mm});
            skLineSegment(sketch, "E111.2.0.28", {"start": v(19.74, -19.05) * mm, "end": v(11.04, -19.05) * mm});
            skLineSegment(sketch, "E111.2.0.29", {"start": v(24.1, -42.56) * mm, "end": v(14.63, -38.06) * mm});
            skPoint(sketch, "E111.2.0.30", {"position": v(9.1, -4.57) * mm});
            skPoint(sketch, "E111.2.0.31", {"position": v(10.37, -28.2) * mm});
            skLineSegment(sketch, "E111.2.0.32", {"start": v(25.4, -44.45) * mm, "end": v(13.81, -38.94) * mm});
            skLineSegment(sketch, "E111.2.0.33", {"start": v(24.1, 42.56) * mm, "end": v(14.63, 38.06) * mm});
            skPoint(sketch, "E111.2.0.34", {"position": v(19.15, -4.57) * mm});
            skPoint(sketch, "E111.2.0.35", {"position": v(12.45, -38.29) * mm});
            skLineSegment(sketch, "E111.2.0.36", {"start": v(9.77, -11.18) * mm, "end": v(18.47, -11.18) * mm});
            skPoint(sketch, "E111.2.0.37", {"position": v(10.37, -19.05) * mm});
            skPoint(sketch, "E111.2.0.38", {"position": v(19.15, 4.57) * mm});
            skPoint(sketch, "E111.2.0.39", {"position": v(19.15, 26.92) * mm});
            skPoint(sketch, "E111.2.0.40", {"position": v(19.15, 11.18) * mm});
            skLineSegment(sketch, "E111.2.0.41", {"start": v(19.74, 19.05) * mm, "end": v(11.04, 19.05) * mm});
            skPoint(sketch, "E111.2.0.42", {"position": v(25.4, 43.18) * mm});
            skPoint(sketch, "E111.2.0.43", {"position": v(25.4, -43.18) * mm});
            skPoint(sketch, "E111.2.0.44", {"position": v(9.1, 11.18) * mm});
            skPoint(sketch, "E111.2.0.45", {"position": v(9.1, 4.57) * mm});
            skLineSegment(sketch, "E111.2.0.46", {"start": v(19.74, 3.3) * mm, "end": v(11.04, 3.3) * mm});
            skLineSegment(sketch, "E111.2.0.47", {"start": v(18.47, 4.57) * mm, "end": v(9.77, 4.57) * mm});
            skPoint(sketch, "E111.2.0.48", {"position": v(19.15, 20.32) * mm});
            skPoint(sketch, "E111.2.0.49", {"position": v(10.37, 19.05) * mm});
            skPoint(sketch, "E111.2.0.50", {"position": v(10.37, 28.2) * mm});
            skPoint(sketch, "E111.2.0.51", {"position": v(10.37, 3.3) * mm});
            skLineSegment(sketch, "E111.2.0.52", {"start": v(18.47, 20.32) * mm, "end": v(9.77, 20.32) * mm});
            skLineSegment(sketch, "E111.2.0.53", {"start": v(10.37, 12.45) * mm, "end": v(19.74, 12.45) * mm});
            skPoint(sketch, "E111.2.0.54", {"position": v(20.42, 28.2) * mm});
            skLineSegment(sketch, "E111.2.0.55", {"start": v(9.77, 11.18) * mm, "end": v(18.47, 11.18) * mm});
            skPoint(sketch, "E111.2.0.56", {"position": v(20.42, 12.45) * mm});
            skPoint(sketch, "E111.2.0.57", {"position": v(20.42, 3.3) * mm});
            skLineSegment(sketch, "E111.2.0.58", {"start": v(29.21, -43.18) * mm, "end": v(26.83, -43.18) * mm});
            skLineSegment(sketch, "E111.2.0.59", {"start": v(25.4, -44.45) * mm, "end": v(29.21, -44.45) * mm});
            skLineSegment(sketch, "E111.2.0.60", {"start": v(9.77, -26.92) * mm, "end": v(18.47, -26.92) * mm});
            skLineSegment(sketch, "E111.2.0.61", {"start": v(29.21, 43.18) * mm, "end": v(26.83, 43.18) * mm});
            skLineSegment(sketch, "E111.2.0.62", {"start": v(29.21, 44.45) * mm, "end": v(29.21, 43.18) * mm});
            skLineSegment(sketch, "E111.2.0.63", {"start": v(20.42, -27.52) * mm, "end": v(20.42, -19.72) * mm});
            skArc(sketch, "E111.2.0.64", {"start": v(14.63, 38.06) * mm, "mid": v(13.27, 37.19) * mm, "end": v(12.18, 36) * mm});
            skLineSegment(sketch, "E111.2.0.65", {"start": v(29.21, -44.45) * mm, "end": v(29.21, -43.18) * mm});
            skLineSegment(sketch, "E111.2.0.66", {"start": v(19.15, -10.5) * mm, "end": v(19.15, -5.24) * mm});
            skArc(sketch, "E111.2.0.67", {"start": v(13.81, -38.94) * mm, "mid": v(12.56, -38.15) * mm, "end": v(11.52, -37.1) * mm});
            skLineSegment(sketch, "E111.2.0.68", {"start": v(9.1, -19.65) * mm, "end": v(9.1, -11.85) * mm});
            skLineSegment(sketch, "E111.2.0.69", {"start": v(12.91, -28.2) * mm, "end": v(19.74, -28.2) * mm});
            skLineSegment(sketch, "E111.2.0.70", {"start": v(19.15, -26.25) * mm, "end": v(19.15, -21) * mm});
            skLineSegment(sketch, "E111.2.0.71", {"start": v(12.91, 28.2) * mm, "end": v(19.74, 28.2) * mm});
            skLineSegment(sketch, "E111.2.0.72", {"start": v(20.42, -11.77) * mm, "end": v(20.42, -3.97) * mm});
            skLineSegment(sketch, "E111.2.0.73", {"start": v(25.4, 44.45) * mm, "end": v(29.21, 44.45) * mm});
            skLineSegment(sketch, "E111.2.0.74", {"start": v(10.37, -18.38) * mm, "end": v(10.37, -12.45) * mm});
            skArc(sketch, "E111.2.0.75", {"start": v(14.63, -38.06) * mm, "mid": v(13.27, -37.19) * mm, "end": v(12.18, -36) * mm});
            skLineSegment(sketch, "E111.2.0.76", {"start": v(9.77, 26.92) * mm, "end": v(18.47, 26.92) * mm});
            skArc(sketch, "E111.2.0.77", {"start": v(10.44, 35.7) * mm, "mid": v(9.44, 33.86) * mm, "end": v(9.1, 31.8) * mm});
            skArc(sketch, "E111.2.0.78", {"start": v(20.42, -27.52) * mm, "mid": v(20.22, -28) * mm, "end": v(19.74, -28.2) * mm});
            skLineSegment(sketch, "E111.2.0.79", {"start": v(20.42, 27.52) * mm, "end": v(20.42, 19.72) * mm});
            skArc(sketch, "E111.2.0.80", {"start": v(18.47, -4.57) * mm, "mid": v(18.95, -4.77) * mm, "end": v(19.15, -5.24) * mm});
            skArc(sketch, "E111.2.0.81", {"start": v(10.44, -35.7) * mm, "mid": v(9.44, -33.86) * mm, "end": v(9.1, -31.8) * mm});
            skArc(sketch, "E111.2.0.82", {"start": v(9.77, -20.32) * mm, "mid": v(9.3, -20.12) * mm, "end": v(9.1, -19.65) * mm});
            skArc(sketch, "E111.2.0.83", {"start": v(19.74, -3.3) * mm, "mid": v(20.22, -3.5) * mm, "end": v(20.42, -3.97) * mm});
            skArc(sketch, "E111.2.0.84", {"start": v(11.55, 35.1) * mm, "mid": v(10.67, 33.36) * mm, "end": v(10.37, 31.43) * mm});
            skLineSegment(sketch, "E111.2.0.85", {"start": v(10.37, 18.38) * mm, "end": v(10.37, 12.45) * mm});
            skArc(sketch, "E111.2.0.86", {"start": v(11.55, -35.1) * mm, "mid": v(10.67, -33.36) * mm, "end": v(10.37, -31.43) * mm});
            skArc(sketch, "E111.2.0.87", {"start": v(10.37, -30.73) * mm, "mid": v(11.11, -28.94) * mm, "end": v(12.91, -28.2) * mm});
            skArc(sketch, "E111.2.0.88", {"start": v(19.15, -10.5) * mm, "mid": v(18.95, -10.98) * mm, "end": v(18.47, -11.18) * mm});
            skArc(sketch, "E111.2.0.89", {"start": v(9.77, 20.32) * mm, "mid": v(9.3, 20.12) * mm, "end": v(9.1, 19.65) * mm});
            skArc(sketch, "E111.2.0.90", {"start": v(13.81, 38.94) * mm, "mid": v(12.56, 38.15) * mm, "end": v(11.52, 37.1) * mm});
            skLineSegment(sketch, "E111.2.0.91", {"start": v(19.15, 10.5) * mm, "end": v(19.15, 5.24) * mm});
            skArc(sketch, "E111.2.0.92", {"start": v(10.37, 30.73) * mm, "mid": v(11.11, 28.94) * mm, "end": v(12.91, 28.2) * mm});
            skArc(sketch, "E111.2.0.93", {"start": v(26.83, 43.18) * mm, "mid": v(25.44, 43.02) * mm, "end": v(24.1, 42.56) * mm});
            skLineSegment(sketch, "E111.2.0.94", {"start": v(12.18, -36) * mm, "end": v(11.55, -35.1) * mm});
            skArc(sketch, "E111.2.0.95", {"start": v(11.04, -19.05) * mm, "mid": v(10.57, -18.85) * mm, "end": v(10.37, -18.38) * mm});
            skArc(sketch, "E111.2.0.96", {"start": v(11.04, 19.05) * mm, "mid": v(10.57, 18.85) * mm, "end": v(10.37, 18.38) * mm});
            skLineSegment(sketch, "E111.2.0.97", {"start": v(9.1, -31.8) * mm, "end": v(9.1, -27.6) * mm});
            skArc(sketch, "E111.2.0.98", {"start": v(20.42, -11.77) * mm, "mid": v(20.22, -12.25) * mm, "end": v(19.74, -12.45) * mm});
            skLineSegment(sketch, "E111.2.0.99", {"start": v(20.42, 11.77) * mm, "end": v(20.42, 3.97) * mm});
            skLineSegment(sketch, "E111.2.0.100", {"start": v(10.37, 31.43) * mm, "end": v(10.37, 30.73) * mm});
            skLineSegment(sketch, "E111.2.0.101", {"start": v(19.15, 26.25) * mm, "end": v(19.15, 21) * mm});
            skArc(sketch, "E111.2.0.102", {"start": v(18.47, -20.32) * mm, "mid": v(18.95, -20.52) * mm, "end": v(19.15, -21) * mm});
            skArc(sketch, "E111.2.0.103", {"start": v(9.1, -11.85) * mm, "mid": v(9.3, -11.37) * mm, "end": v(9.77, -11.18) * mm});
            skLineSegment(sketch, "E111.2.0.104", {"start": v(11.52, 37.1) * mm, "end": v(10.44, 35.7) * mm});
            skLineSegment(sketch, "E111.2.0.105", {"start": v(9.1, 31.8) * mm, "end": v(9.1, 27.6) * mm});
            skArc(sketch, "E111.2.0.106", {"start": v(26.83, -43.18) * mm, "mid": v(25.44, -43.02) * mm, "end": v(24.1, -42.56) * mm});
            skArc(sketch, "E111.2.0.107", {"start": v(19.74, -19.05) * mm, "mid": v(20.22, -19.25) * mm, "end": v(20.42, -19.72) * mm});
            skLineSegment(sketch, "E111.2.0.108", {"start": v(11.52, -37.1) * mm, "end": v(10.44, -35.7) * mm});
            skLineSegment(sketch, "E111.2.0.109", {"start": v(12.18, 36) * mm, "end": v(11.55, 35.1) * mm});
            skLineSegment(sketch, "E111.2.0.110", {"start": v(9.1, 19.65) * mm, "end": v(9.1, 11.85) * mm});
            skArc(sketch, "E111.2.0.111", {"start": v(19.15, -26.25) * mm, "mid": v(18.95, -26.73) * mm, "end": v(18.47, -26.92) * mm});
            skArc(sketch, "E111.2.0.112", {"start": v(9.1, -27.6) * mm, "mid": v(9.3, -27.12) * mm, "end": v(9.77, -26.92) * mm});
            skArc(sketch, "E111.2.0.113", {"start": v(18.47, 20.32) * mm, "mid": v(18.95, 20.52) * mm, "end": v(19.15, 21) * mm});
            skLineSegment(sketch, "E111.2.0.114", {"start": v(10.37, -2.63) * mm, "end": v(10.37, 0) * mm});
            skArc(sketch, "E111.2.0.115", {"start": v(11.04, 3.3) * mm, "mid": v(10.57, 3.1) * mm, "end": v(10.37, 2.63) * mm});
            skArc(sketch, "E111.2.0.116", {"start": v(19.74, 19.05) * mm, "mid": v(20.22, 19.25) * mm, "end": v(20.42, 19.72) * mm});
            skArc(sketch, "E111.2.0.117", {"start": v(18.47, 4.57) * mm, "mid": v(18.95, 4.77) * mm, "end": v(19.15, 5.24) * mm});
            skArc(sketch, "E111.2.0.118", {"start": v(19.74, 3.3) * mm, "mid": v(20.22, 3.5) * mm, "end": v(20.42, 3.97) * mm});
            skArc(sketch, "E111.2.0.119", {"start": v(20.42, 11.77) * mm, "mid": v(20.22, 12.25) * mm, "end": v(19.74, 12.45) * mm});
            skLineSegment(sketch, "E111.2.0.120", {"start": v(10.37, -31.43) * mm, "end": v(10.37, -30.73) * mm});
            skLineSegment(sketch, "E111.2.0.121", {"start": v(9.1, -3.9) * mm, "end": v(9.1, 0) * mm});
            skArc(sketch, "E111.2.0.122", {"start": v(20.42, 27.52) * mm, "mid": v(20.22, 28) * mm, "end": v(19.74, 28.2) * mm});
            skArc(sketch, "E111.2.0.123", {"start": v(19.15, 26.25) * mm, "mid": v(18.95, 26.73) * mm, "end": v(18.47, 26.92) * mm});
            skArc(sketch, "E111.2.0.124", {"start": v(9.77, -4.57) * mm, "mid": v(9.3, -4.38) * mm, "end": v(9.1, -3.9) * mm});
            skArc(sketch, "E111.2.0.125", {"start": v(11.04, -3.3) * mm, "mid": v(10.57, -3.1) * mm, "end": v(10.37, -2.63) * mm});
            skArc(sketch, "E111.2.0.126", {"start": v(9.1, 11.85) * mm, "mid": v(9.3, 11.37) * mm, "end": v(9.77, 11.18) * mm});
            skArc(sketch, "E111.2.0.127", {"start": v(9.77, 4.57) * mm, "mid": v(9.3, 4.38) * mm, "end": v(9.1, 3.9) * mm});
            skArc(sketch, "E111.2.0.128", {"start": v(9.1, 27.6) * mm, "mid": v(9.3, 27.12) * mm, "end": v(9.77, 26.92) * mm});
            skLineSegment(sketch, "E111.2.0.129", {"start": v(10.37, 2.63) * mm, "end": v(10.37, 0) * mm});
            skArc(sketch, "E111.2.0.130", {"start": v(19.15, 10.5) * mm, "mid": v(18.95, 10.98) * mm, "end": v(18.47, 11.18) * mm});
            skLineSegment(sketch, "E111.2.0.131", {"start": v(9.1, 3.9) * mm, "end": v(9.1, 0) * mm});
            skPoint(sketch, "E111.3.0.0", {"position": v(23.07, 33.45) * mm});
            skPoint(sketch, "E111.3.0.1", {"position": v(33.12, 19.05) * mm});
            skPoint(sketch, "E111.3.0.2", {"position": v(21.8, -26.92) * mm});
            skLineSegment(sketch, "E111.3.0.3", {"start": v(23.07, -12.45) * mm, "end": v(32.44, -12.45) * mm});
            skLineSegment(sketch, "E111.3.0.4", {"start": v(31.17, -20.32) * mm, "end": v(22.47, -20.32) * mm});
            skPoint(sketch, "E111.3.0.5", {"position": v(21.8, -33.98) * mm});
            skPoint(sketch, "E111.3.0.6", {"position": v(25.15, 38.29) * mm});
            skPoint(sketch, "E111.3.0.7", {"position": v(25.84, -37.35) * mm});
            skPoint(sketch, "E111.3.0.8", {"position": v(21.8, -11.18) * mm});
            skLineSegment(sketch, "E111.3.0.9", {"start": v(32.44, -3.3) * mm, "end": v(23.74, -3.3) * mm});
            skPoint(sketch, "E111.3.0.10", {"position": v(21.8, 20.32) * mm});
            skPoint(sketch, "E111.3.0.11", {"position": v(21.8, -20.32) * mm});
            skPoint(sketch, "E111.3.0.12", {"position": v(21.8, 33.98) * mm});
            skPoint(sketch, "E111.3.0.13", {"position": v(33.12, -3.3) * mm});
            skPoint(sketch, "E111.3.0.14", {"position": v(31.85, -11.18) * mm});
            skPoint(sketch, "E111.3.0.15", {"position": v(33.12, -12.45) * mm});
            skLineSegment(sketch, "E111.3.0.16", {"start": v(31.17, -4.57) * mm, "end": v(22.47, -4.57) * mm});
            skPoint(sketch, "E111.3.0.17", {"position": v(38.1, -43.18) * mm});
            skPoint(sketch, "E111.3.0.18", {"position": v(33.12, -19.05) * mm});
            skPoint(sketch, "E111.3.0.19", {"position": v(38.1, 43.18) * mm});
            skPoint(sketch, "E111.3.0.20", {"position": v(33.12, -28.2) * mm});
            skPoint(sketch, "E111.3.0.21", {"position": v(21.8, 26.92) * mm});
            skPoint(sketch, "E111.3.0.22", {"position": v(25.84, 37.35) * mm});
            skPoint(sketch, "E111.3.0.23", {"position": v(23.07, -33.45) * mm});
            skLineSegment(sketch, "E111.3.0.24", {"start": v(38.1, 44.45) * mm, "end": v(26.51, 38.94) * mm});
            skPoint(sketch, "E111.3.0.25", {"position": v(31.85, -20.32) * mm});
            skPoint(sketch, "E111.3.0.26", {"position": v(23.07, -3.3) * mm});
            skPoint(sketch, "E111.3.0.27", {"position": v(31.85, -26.92) * mm});
            skLineSegment(sketch, "E111.3.0.28", {"start": v(32.44, -19.05) * mm, "end": v(23.74, -19.05) * mm});
            skLineSegment(sketch, "E111.3.0.29", {"start": v(36.8, -42.56) * mm, "end": v(27.33, -38.06) * mm});
            skPoint(sketch, "E111.3.0.30", {"position": v(21.8, -4.57) * mm});
            skPoint(sketch, "E111.3.0.31", {"position": v(23.07, -28.2) * mm});
            skLineSegment(sketch, "E111.3.0.32", {"start": v(38.1, -44.45) * mm, "end": v(26.51, -38.94) * mm});
            skLineSegment(sketch, "E111.3.0.33", {"start": v(36.8, 42.56) * mm, "end": v(27.33, 38.06) * mm});
            skPoint(sketch, "E111.3.0.34", {"position": v(31.85, -4.57) * mm});
            skPoint(sketch, "E111.3.0.35", {"position": v(25.15, -38.29) * mm});
            skLineSegment(sketch, "E111.3.0.36", {"start": v(22.47, -11.18) * mm, "end": v(31.17, -11.18) * mm});
            skPoint(sketch, "E111.3.0.37", {"position": v(23.07, -19.05) * mm});
            skPoint(sketch, "E111.3.0.38", {"position": v(31.85, 4.57) * mm});
            skPoint(sketch, "E111.3.0.39", {"position": v(31.85, 26.92) * mm});
            skPoint(sketch, "E111.3.0.40", {"position": v(31.85, 11.18) * mm});
            skLineSegment(sketch, "E111.3.0.41", {"start": v(32.44, 19.05) * mm, "end": v(23.74, 19.05) * mm});
            skPoint(sketch, "E111.3.0.42", {"position": v(38.1, 43.18) * mm});
            skPoint(sketch, "E111.3.0.43", {"position": v(38.1, -43.18) * mm});
            skPoint(sketch, "E111.3.0.44", {"position": v(21.8, 11.18) * mm});
            skPoint(sketch, "E111.3.0.45", {"position": v(21.8, 4.57) * mm});
            skLineSegment(sketch, "E111.3.0.46", {"start": v(32.44, 3.3) * mm, "end": v(23.74, 3.3) * mm});
            skLineSegment(sketch, "E111.3.0.47", {"start": v(31.17, 4.57) * mm, "end": v(22.47, 4.57) * mm});
            skPoint(sketch, "E111.3.0.48", {"position": v(31.85, 20.32) * mm});
            skPoint(sketch, "E111.3.0.49", {"position": v(23.07, 19.05) * mm});
            skPoint(sketch, "E111.3.0.50", {"position": v(23.07, 28.2) * mm});
            skPoint(sketch, "E111.3.0.51", {"position": v(23.07, 3.3) * mm});
            skLineSegment(sketch, "E111.3.0.52", {"start": v(31.17, 20.32) * mm, "end": v(22.47, 20.32) * mm});
            skLineSegment(sketch, "E111.3.0.53", {"start": v(23.07, 12.45) * mm, "end": v(32.44, 12.45) * mm});
            skPoint(sketch, "E111.3.0.54", {"position": v(33.12, 28.2) * mm});
            skLineSegment(sketch, "E111.3.0.55", {"start": v(22.47, 11.18) * mm, "end": v(31.17, 11.18) * mm});
            skPoint(sketch, "E111.3.0.56", {"position": v(33.12, 12.45) * mm});
            skPoint(sketch, "E111.3.0.57", {"position": v(33.12, 3.3) * mm});
            skLineSegment(sketch, "E111.3.0.58", {"start": v(41.91, -43.18) * mm, "end": v(39.53, -43.18) * mm});
            skLineSegment(sketch, "E111.3.0.59", {"start": v(38.1, -44.45) * mm, "end": v(41.91, -44.45) * mm});
            skLineSegment(sketch, "E111.3.0.60", {"start": v(22.47, -26.92) * mm, "end": v(31.17, -26.92) * mm});
            skLineSegment(sketch, "E111.3.0.61", {"start": v(41.91, 43.18) * mm, "end": v(39.53, 43.18) * mm});
            skLineSegment(sketch, "E111.3.0.62", {"start": v(41.91, 44.45) * mm, "end": v(41.91, 43.18) * mm});
            skLineSegment(sketch, "E111.3.0.63", {"start": v(33.12, -27.52) * mm, "end": v(33.12, -19.72) * mm});
            skArc(sketch, "E111.3.0.64", {"start": v(27.33, 38.06) * mm, "mid": v(25.97, 37.19) * mm, "end": v(24.88, 36) * mm});
            skLineSegment(sketch, "E111.3.0.65", {"start": v(41.91, -44.45) * mm, "end": v(41.91, -43.18) * mm});
            skLineSegment(sketch, "E111.3.0.66", {"start": v(31.85, -10.5) * mm, "end": v(31.85, -5.24) * mm});
            skArc(sketch, "E111.3.0.67", {"start": v(26.51, -38.94) * mm, "mid": v(25.26, -38.15) * mm, "end": v(24.22, -37.1) * mm});
            skLineSegment(sketch, "E111.3.0.68", {"start": v(21.8, -19.65) * mm, "end": v(21.8, -11.85) * mm});
            skLineSegment(sketch, "E111.3.0.69", {"start": v(25.61, -28.2) * mm, "end": v(32.44, -28.2) * mm});
            skLineSegment(sketch, "E111.3.0.70", {"start": v(31.85, -26.25) * mm, "end": v(31.85, -21) * mm});
            skLineSegment(sketch, "E111.3.0.71", {"start": v(25.61, 28.2) * mm, "end": v(32.44, 28.2) * mm});
            skLineSegment(sketch, "E111.3.0.72", {"start": v(33.12, -11.77) * mm, "end": v(33.12, -3.97) * mm});
            skLineSegment(sketch, "E111.3.0.73", {"start": v(38.1, 44.45) * mm, "end": v(41.91, 44.45) * mm});
            skLineSegment(sketch, "E111.3.0.74", {"start": v(23.07, -18.38) * mm, "end": v(23.07, -12.45) * mm});
            skArc(sketch, "E111.3.0.75", {"start": v(27.33, -38.06) * mm, "mid": v(25.97, -37.19) * mm, "end": v(24.88, -36) * mm});
            skLineSegment(sketch, "E111.3.0.76", {"start": v(22.47, 26.92) * mm, "end": v(31.17, 26.92) * mm});
            skArc(sketch, "E111.3.0.77", {"start": v(23.14, 35.7) * mm, "mid": v(22.14, 33.86) * mm, "end": v(21.8, 31.8) * mm});
            skArc(sketch, "E111.3.0.78", {"start": v(33.12, -27.52) * mm, "mid": v(32.92, -28) * mm, "end": v(32.44, -28.2) * mm});
            skLineSegment(sketch, "E111.3.0.79", {"start": v(33.12, 27.52) * mm, "end": v(33.12, 19.72) * mm});
            skArc(sketch, "E111.3.0.80", {"start": v(31.17, -4.57) * mm, "mid": v(31.65, -4.77) * mm, "end": v(31.85, -5.24) * mm});
            skArc(sketch, "E111.3.0.81", {"start": v(23.14, -35.7) * mm, "mid": v(22.14, -33.86) * mm, "end": v(21.8, -31.8) * mm});
            skArc(sketch, "E111.3.0.82", {"start": v(22.47, -20.32) * mm, "mid": v(22, -20.12) * mm, "end": v(21.8, -19.65) * mm});
            skArc(sketch, "E111.3.0.83", {"start": v(32.44, -3.3) * mm, "mid": v(32.92, -3.5) * mm, "end": v(33.12, -3.97) * mm});
            skArc(sketch, "E111.3.0.84", {"start": v(24.25, 35.1) * mm, "mid": v(23.37, 33.36) * mm, "end": v(23.07, 31.43) * mm});
            skLineSegment(sketch, "E111.3.0.85", {"start": v(23.07, 18.38) * mm, "end": v(23.07, 12.45) * mm});
            skArc(sketch, "E111.3.0.86", {"start": v(24.25, -35.1) * mm, "mid": v(23.37, -33.36) * mm, "end": v(23.07, -31.43) * mm});
            skArc(sketch, "E111.3.0.87", {"start": v(23.07, -30.73) * mm, "mid": v(23.81, -28.94) * mm, "end": v(25.61, -28.2) * mm});
            skArc(sketch, "E111.3.0.88", {"start": v(31.85, -10.5) * mm, "mid": v(31.65, -10.98) * mm, "end": v(31.17, -11.18) * mm});
            skArc(sketch, "E111.3.0.89", {"start": v(22.47, 20.32) * mm, "mid": v(22, 20.12) * mm, "end": v(21.8, 19.65) * mm});
            skArc(sketch, "E111.3.0.90", {"start": v(26.51, 38.94) * mm, "mid": v(25.26, 38.15) * mm, "end": v(24.22, 37.1) * mm});
            skLineSegment(sketch, "E111.3.0.91", {"start": v(31.85, 10.5) * mm, "end": v(31.85, 5.24) * mm});
            skArc(sketch, "E111.3.0.92", {"start": v(23.07, 30.73) * mm, "mid": v(23.81, 28.94) * mm, "end": v(25.61, 28.2) * mm});
            skArc(sketch, "E111.3.0.93", {"start": v(39.53, 43.18) * mm, "mid": v(38.14, 43.02) * mm, "end": v(36.8, 42.56) * mm});
            skLineSegment(sketch, "E111.3.0.94", {"start": v(24.88, -36) * mm, "end": v(24.25, -35.1) * mm});
            skArc(sketch, "E111.3.0.95", {"start": v(23.74, -19.05) * mm, "mid": v(23.27, -18.85) * mm, "end": v(23.07, -18.38) * mm});
            skArc(sketch, "E111.3.0.96", {"start": v(23.74, 19.05) * mm, "mid": v(23.27, 18.85) * mm, "end": v(23.07, 18.38) * mm});
            skLineSegment(sketch, "E111.3.0.97", {"start": v(21.8, -31.8) * mm, "end": v(21.8, -27.6) * mm});
            skArc(sketch, "E111.3.0.98", {"start": v(33.12, -11.77) * mm, "mid": v(32.92, -12.25) * mm, "end": v(32.44, -12.45) * mm});
            skLineSegment(sketch, "E111.3.0.99", {"start": v(33.12, 11.77) * mm, "end": v(33.12, 3.97) * mm});
            skLineSegment(sketch, "E111.3.0.100", {"start": v(23.07, 31.43) * mm, "end": v(23.07, 30.73) * mm});
            skLineSegment(sketch, "E111.3.0.101", {"start": v(31.85, 26.25) * mm, "end": v(31.85, 21) * mm});
            skArc(sketch, "E111.3.0.102", {"start": v(31.17, -20.32) * mm, "mid": v(31.65, -20.52) * mm, "end": v(31.85, -21) * mm});
            skArc(sketch, "E111.3.0.103", {"start": v(21.8, -11.85) * mm, "mid": v(22, -11.37) * mm, "end": v(22.47, -11.18) * mm});
            skLineSegment(sketch, "E111.3.0.104", {"start": v(24.22, 37.1) * mm, "end": v(23.14, 35.7) * mm});
            skLineSegment(sketch, "E111.3.0.105", {"start": v(21.8, 31.8) * mm, "end": v(21.8, 27.6) * mm});
            skArc(sketch, "E111.3.0.106", {"start": v(39.53, -43.18) * mm, "mid": v(38.14, -43.02) * mm, "end": v(36.8, -42.56) * mm});
            skArc(sketch, "E111.3.0.107", {"start": v(32.44, -19.05) * mm, "mid": v(32.92, -19.25) * mm, "end": v(33.12, -19.72) * mm});
            skLineSegment(sketch, "E111.3.0.108", {"start": v(24.22, -37.1) * mm, "end": v(23.14, -35.7) * mm});
            skLineSegment(sketch, "E111.3.0.109", {"start": v(24.88, 36) * mm, "end": v(24.25, 35.1) * mm});
            skLineSegment(sketch, "E111.3.0.110", {"start": v(21.8, 19.65) * mm, "end": v(21.8, 11.85) * mm});
            skArc(sketch, "E111.3.0.111", {"start": v(31.85, -26.25) * mm, "mid": v(31.65, -26.73) * mm, "end": v(31.17, -26.92) * mm});
            skArc(sketch, "E111.3.0.112", {"start": v(21.8, -27.6) * mm, "mid": v(22, -27.12) * mm, "end": v(22.47, -26.92) * mm});
            skArc(sketch, "E111.3.0.113", {"start": v(31.17, 20.32) * mm, "mid": v(31.65, 20.52) * mm, "end": v(31.85, 21) * mm});
            skLineSegment(sketch, "E111.3.0.114", {"start": v(23.07, -2.63) * mm, "end": v(23.07, 0) * mm});
            skArc(sketch, "E111.3.0.115", {"start": v(23.74, 3.3) * mm, "mid": v(23.27, 3.1) * mm, "end": v(23.07, 2.63) * mm});
            skArc(sketch, "E111.3.0.116", {"start": v(32.44, 19.05) * mm, "mid": v(32.92, 19.25) * mm, "end": v(33.12, 19.72) * mm});
            skArc(sketch, "E111.3.0.117", {"start": v(31.17, 4.57) * mm, "mid": v(31.65, 4.77) * mm, "end": v(31.85, 5.24) * mm});
            skArc(sketch, "E111.3.0.118", {"start": v(32.44, 3.3) * mm, "mid": v(32.92, 3.5) * mm, "end": v(33.12, 3.97) * mm});
            skArc(sketch, "E111.3.0.119", {"start": v(33.12, 11.77) * mm, "mid": v(32.92, 12.25) * mm, "end": v(32.44, 12.45) * mm});
            skLineSegment(sketch, "E111.3.0.120", {"start": v(23.07, -31.43) * mm, "end": v(23.07, -30.73) * mm});
            skLineSegment(sketch, "E111.3.0.121", {"start": v(21.8, -3.9) * mm, "end": v(21.8, 0) * mm});
            skArc(sketch, "E111.3.0.122", {"start": v(33.12, 27.52) * mm, "mid": v(32.92, 28) * mm, "end": v(32.44, 28.2) * mm});
            skArc(sketch, "E111.3.0.123", {"start": v(31.85, 26.25) * mm, "mid": v(31.65, 26.73) * mm, "end": v(31.17, 26.92) * mm});
            skArc(sketch, "E111.3.0.124", {"start": v(22.47, -4.57) * mm, "mid": v(22, -4.38) * mm, "end": v(21.8, -3.9) * mm});
            skArc(sketch, "E111.3.0.125", {"start": v(23.74, -3.3) * mm, "mid": v(23.27, -3.1) * mm, "end": v(23.07, -2.63) * mm});
            skArc(sketch, "E111.3.0.126", {"start": v(21.8, 11.85) * mm, "mid": v(22, 11.37) * mm, "end": v(22.47, 11.18) * mm});
            skArc(sketch, "E111.3.0.127", {"start": v(22.47, 4.57) * mm, "mid": v(22, 4.38) * mm, "end": v(21.8, 3.9) * mm});
            skArc(sketch, "E111.3.0.128", {"start": v(21.8, 27.6) * mm, "mid": v(22, 27.12) * mm, "end": v(22.47, 26.92) * mm});
            skLineSegment(sketch, "E111.3.0.129", {"start": v(23.07, 2.63) * mm, "end": v(23.07, 0) * mm});
            skArc(sketch, "E111.3.0.130", {"start": v(31.85, 10.5) * mm, "mid": v(31.65, 10.98) * mm, "end": v(31.17, 11.18) * mm});
            skLineSegment(sketch, "E111.3.0.131", {"start": v(21.8, 3.9) * mm, "end": v(21.8, 0) * mm});
            skPoint(sketch, "E111.4.0.0", {"position": v(35.77, 33.45) * mm});
            skPoint(sketch, "E111.4.0.1", {"position": v(45.82, 19.05) * mm});
            skPoint(sketch, "E111.4.0.2", {"position": v(34.5, -26.92) * mm});
            skLineSegment(sketch, "E111.4.0.3", {"start": v(35.77, -12.45) * mm, "end": v(45.14, -12.45) * mm});
            skLineSegment(sketch, "E111.4.0.4", {"start": v(43.87, -20.32) * mm, "end": v(35.17, -20.32) * mm});
            skPoint(sketch, "E111.4.0.5", {"position": v(34.5, -33.98) * mm});
            skPoint(sketch, "E111.4.0.6", {"position": v(37.85, 38.29) * mm});
            skPoint(sketch, "E111.4.0.7", {"position": v(38.54, -37.35) * mm});
            skPoint(sketch, "E111.4.0.8", {"position": v(34.5, -11.18) * mm});
            skLineSegment(sketch, "E111.4.0.9", {"start": v(45.14, -3.3) * mm, "end": v(36.44, -3.3) * mm});
            skPoint(sketch, "E111.4.0.10", {"position": v(34.5, 20.32) * mm});
            skPoint(sketch, "E111.4.0.11", {"position": v(34.5, -20.32) * mm});
            skPoint(sketch, "E111.4.0.12", {"position": v(34.5, 33.98) * mm});
            skPoint(sketch, "E111.4.0.13", {"position": v(45.82, -3.3) * mm});
            skPoint(sketch, "E111.4.0.14", {"position": v(44.55, -11.18) * mm});
            skPoint(sketch, "E111.4.0.15", {"position": v(45.82, -12.45) * mm});
            skLineSegment(sketch, "E111.4.0.16", {"start": v(43.87, -4.57) * mm, "end": v(35.17, -4.57) * mm});
            skPoint(sketch, "E111.4.0.17", {"position": v(50.8, -43.18) * mm});
            skPoint(sketch, "E111.4.0.18", {"position": v(45.82, -19.05) * mm});
            skPoint(sketch, "E111.4.0.19", {"position": v(50.8, 43.18) * mm});
            skPoint(sketch, "E111.4.0.20", {"position": v(45.82, -28.2) * mm});
            skPoint(sketch, "E111.4.0.21", {"position": v(34.5, 26.92) * mm});
            skPoint(sketch, "E111.4.0.22", {"position": v(38.54, 37.35) * mm});
            skPoint(sketch, "E111.4.0.23", {"position": v(35.77, -33.45) * mm});
            skLineSegment(sketch, "E111.4.0.24", {"start": v(50.8, 44.45) * mm, "end": v(39.21, 38.94) * mm});
            skPoint(sketch, "E111.4.0.25", {"position": v(44.55, -20.32) * mm});
            skPoint(sketch, "E111.4.0.26", {"position": v(35.77, -3.3) * mm});
            skPoint(sketch, "E111.4.0.27", {"position": v(44.55, -26.92) * mm});
            skLineSegment(sketch, "E111.4.0.28", {"start": v(45.14, -19.05) * mm, "end": v(36.44, -19.05) * mm});
            skLineSegment(sketch, "E111.4.0.29", {"start": v(49.5, -42.56) * mm, "end": v(40.03, -38.06) * mm});
            skPoint(sketch, "E111.4.0.30", {"position": v(34.5, -4.57) * mm});
            skPoint(sketch, "E111.4.0.31", {"position": v(35.77, -28.2) * mm});
            skLineSegment(sketch, "E111.4.0.32", {"start": v(50.8, -44.45) * mm, "end": v(39.21, -38.94) * mm});
            skLineSegment(sketch, "E111.4.0.33", {"start": v(49.5, 42.56) * mm, "end": v(40.03, 38.06) * mm});
            skPoint(sketch, "E111.4.0.34", {"position": v(44.55, -4.57) * mm});
            skPoint(sketch, "E111.4.0.35", {"position": v(37.85, -38.29) * mm});
            skLineSegment(sketch, "E111.4.0.36", {"start": v(35.17, -11.18) * mm, "end": v(43.87, -11.18) * mm});
            skPoint(sketch, "E111.4.0.37", {"position": v(35.77, -19.05) * mm});
            skPoint(sketch, "E111.4.0.38", {"position": v(44.55, 4.57) * mm});
            skPoint(sketch, "E111.4.0.39", {"position": v(44.55, 26.92) * mm});
            skPoint(sketch, "E111.4.0.40", {"position": v(44.55, 11.18) * mm});
            skLineSegment(sketch, "E111.4.0.41", {"start": v(45.14, 19.05) * mm, "end": v(36.44, 19.05) * mm});
            skPoint(sketch, "E111.4.0.42", {"position": v(50.8, 43.18) * mm});
            skPoint(sketch, "E111.4.0.43", {"position": v(50.8, -43.18) * mm});
            skPoint(sketch, "E111.4.0.44", {"position": v(34.5, 11.18) * mm});
            skPoint(sketch, "E111.4.0.45", {"position": v(34.5, 4.57) * mm});
            skLineSegment(sketch, "E111.4.0.46", {"start": v(45.14, 3.3) * mm, "end": v(36.44, 3.3) * mm});
            skLineSegment(sketch, "E111.4.0.47", {"start": v(43.87, 4.57) * mm, "end": v(35.17, 4.57) * mm});
            skPoint(sketch, "E111.4.0.48", {"position": v(44.55, 20.32) * mm});
            skPoint(sketch, "E111.4.0.49", {"position": v(35.77, 19.05) * mm});
            skPoint(sketch, "E111.4.0.50", {"position": v(35.77, 28.2) * mm});
            skPoint(sketch, "E111.4.0.51", {"position": v(35.77, 3.3) * mm});
            skLineSegment(sketch, "E111.4.0.52", {"start": v(43.87, 20.32) * mm, "end": v(35.17, 20.32) * mm});
            skLineSegment(sketch, "E111.4.0.53", {"start": v(35.77, 12.45) * mm, "end": v(45.14, 12.45) * mm});
            skPoint(sketch, "E111.4.0.54", {"position": v(45.82, 28.2) * mm});
            skLineSegment(sketch, "E111.4.0.55", {"start": v(35.17, 11.18) * mm, "end": v(43.87, 11.18) * mm});
            skPoint(sketch, "E111.4.0.56", {"position": v(45.82, 12.45) * mm});
            skPoint(sketch, "E111.4.0.57", {"position": v(45.82, 3.3) * mm});
            skLineSegment(sketch, "E111.4.0.58", {"start": v(54.61, -43.18) * mm, "end": v(52.23, -43.18) * mm});
            skLineSegment(sketch, "E111.4.0.59", {"start": v(50.8, -44.45) * mm, "end": v(54.61, -44.45) * mm});
            skLineSegment(sketch, "E111.4.0.60", {"start": v(35.17, -26.92) * mm, "end": v(43.87, -26.92) * mm});
            skLineSegment(sketch, "E111.4.0.61", {"start": v(54.61, 43.18) * mm, "end": v(52.23, 43.18) * mm});
            skLineSegment(sketch, "E111.4.0.62", {"start": v(54.61, 44.45) * mm, "end": v(54.61, 43.18) * mm});
            skLineSegment(sketch, "E111.4.0.63", {"start": v(45.82, -27.52) * mm, "end": v(45.82, -19.72) * mm});
            skArc(sketch, "E111.4.0.64", {"start": v(40.03, 38.06) * mm, "mid": v(38.67, 37.19) * mm, "end": v(37.58, 36) * mm});
            skLineSegment(sketch, "E111.4.0.65", {"start": v(54.61, -44.45) * mm, "end": v(54.61, -43.18) * mm});
            skLineSegment(sketch, "E111.4.0.66", {"start": v(44.55, -10.5) * mm, "end": v(44.55, -5.24) * mm});
            skArc(sketch, "E111.4.0.67", {"start": v(39.21, -38.94) * mm, "mid": v(37.96, -38.15) * mm, "end": v(36.92, -37.1) * mm});
            skLineSegment(sketch, "E111.4.0.68", {"start": v(34.5, -19.65) * mm, "end": v(34.5, -11.85) * mm});
            skLineSegment(sketch, "E111.4.0.69", {"start": v(38.31, -28.2) * mm, "end": v(45.14, -28.2) * mm});
            skLineSegment(sketch, "E111.4.0.70", {"start": v(44.55, -26.25) * mm, "end": v(44.55, -21) * mm});
            skLineSegment(sketch, "E111.4.0.71", {"start": v(38.31, 28.2) * mm, "end": v(45.14, 28.2) * mm});
            skLineSegment(sketch, "E111.4.0.72", {"start": v(45.82, -11.77) * mm, "end": v(45.82, -3.97) * mm});
            skLineSegment(sketch, "E111.4.0.73", {"start": v(50.8, 44.45) * mm, "end": v(54.61, 44.45) * mm});
            skLineSegment(sketch, "E111.4.0.74", {"start": v(35.77, -18.38) * mm, "end": v(35.77, -12.45) * mm});
            skArc(sketch, "E111.4.0.75", {"start": v(40.03, -38.06) * mm, "mid": v(38.67, -37.19) * mm, "end": v(37.58, -36) * mm});
            skLineSegment(sketch, "E111.4.0.76", {"start": v(35.17, 26.92) * mm, "end": v(43.87, 26.92) * mm});
            skArc(sketch, "E111.4.0.77", {"start": v(35.84, 35.7) * mm, "mid": v(34.84, 33.86) * mm, "end": v(34.5, 31.8) * mm});
            skArc(sketch, "E111.4.0.78", {"start": v(45.82, -27.52) * mm, "mid": v(45.62, -28) * mm, "end": v(45.14, -28.2) * mm});
            skLineSegment(sketch, "E111.4.0.79", {"start": v(45.82, 27.52) * mm, "end": v(45.82, 19.72) * mm});
            skArc(sketch, "E111.4.0.80", {"start": v(43.87, -4.57) * mm, "mid": v(44.35, -4.77) * mm, "end": v(44.55, -5.24) * mm});
            skArc(sketch, "E111.4.0.81", {"start": v(35.84, -35.7) * mm, "mid": v(34.84, -33.86) * mm, "end": v(34.5, -31.8) * mm});
            skArc(sketch, "E111.4.0.82", {"start": v(35.17, -20.32) * mm, "mid": v(34.7, -20.12) * mm, "end": v(34.5, -19.65) * mm});
            skArc(sketch, "E111.4.0.83", {"start": v(45.14, -3.3) * mm, "mid": v(45.62, -3.5) * mm, "end": v(45.82, -3.97) * mm});
            skArc(sketch, "E111.4.0.84", {"start": v(36.95, 35.1) * mm, "mid": v(36.07, 33.36) * mm, "end": v(35.77, 31.43) * mm});
            skLineSegment(sketch, "E111.4.0.85", {"start": v(35.77, 18.38) * mm, "end": v(35.77, 12.45) * mm});
            skArc(sketch, "E111.4.0.86", {"start": v(36.95, -35.1) * mm, "mid": v(36.07, -33.36) * mm, "end": v(35.77, -31.43) * mm});
            skArc(sketch, "E111.4.0.87", {"start": v(35.77, -30.73) * mm, "mid": v(36.51, -28.94) * mm, "end": v(38.31, -28.2) * mm});
            skArc(sketch, "E111.4.0.88", {"start": v(44.55, -10.5) * mm, "mid": v(44.35, -10.98) * mm, "end": v(43.87, -11.18) * mm});
            skArc(sketch, "E111.4.0.89", {"start": v(35.17, 20.32) * mm, "mid": v(34.7, 20.12) * mm, "end": v(34.5, 19.65) * mm});
            skArc(sketch, "E111.4.0.90", {"start": v(39.21, 38.94) * mm, "mid": v(37.96, 38.15) * mm, "end": v(36.92, 37.1) * mm});
            skLineSegment(sketch, "E111.4.0.91", {"start": v(44.55, 10.5) * mm, "end": v(44.55, 5.24) * mm});
            skArc(sketch, "E111.4.0.92", {"start": v(35.77, 30.73) * mm, "mid": v(36.51, 28.94) * mm, "end": v(38.31, 28.2) * mm});
            skArc(sketch, "E111.4.0.93", {"start": v(52.23, 43.18) * mm, "mid": v(50.84, 43.02) * mm, "end": v(49.5, 42.56) * mm});
            skLineSegment(sketch, "E111.4.0.94", {"start": v(37.58, -36) * mm, "end": v(36.95, -35.1) * mm});
            skArc(sketch, "E111.4.0.95", {"start": v(36.44, -19.05) * mm, "mid": v(35.97, -18.85) * mm, "end": v(35.77, -18.38) * mm});
            skArc(sketch, "E111.4.0.96", {"start": v(36.44, 19.05) * mm, "mid": v(35.97, 18.85) * mm, "end": v(35.77, 18.38) * mm});
            skLineSegment(sketch, "E111.4.0.97", {"start": v(34.5, -31.8) * mm, "end": v(34.5, -27.6) * mm});
            skArc(sketch, "E111.4.0.98", {"start": v(45.82, -11.77) * mm, "mid": v(45.62, -12.25) * mm, "end": v(45.14, -12.45) * mm});
            skLineSegment(sketch, "E111.4.0.99", {"start": v(45.82, 11.77) * mm, "end": v(45.82, 3.97) * mm});
            skLineSegment(sketch, "E111.4.0.100", {"start": v(35.77, 31.43) * mm, "end": v(35.77, 30.73) * mm});
            skLineSegment(sketch, "E111.4.0.101", {"start": v(44.55, 26.25) * mm, "end": v(44.55, 21) * mm});
            skArc(sketch, "E111.4.0.102", {"start": v(43.87, -20.32) * mm, "mid": v(44.35, -20.52) * mm, "end": v(44.55, -21) * mm});
            skArc(sketch, "E111.4.0.103", {"start": v(34.5, -11.85) * mm, "mid": v(34.7, -11.37) * mm, "end": v(35.17, -11.18) * mm});
            skLineSegment(sketch, "E111.4.0.104", {"start": v(36.92, 37.1) * mm, "end": v(35.84, 35.7) * mm});
            skLineSegment(sketch, "E111.4.0.105", {"start": v(34.5, 31.8) * mm, "end": v(34.5, 27.6) * mm});
            skArc(sketch, "E111.4.0.106", {"start": v(52.23, -43.18) * mm, "mid": v(50.84, -43.02) * mm, "end": v(49.5, -42.56) * mm});
            skArc(sketch, "E111.4.0.107", {"start": v(45.14, -19.05) * mm, "mid": v(45.62, -19.25) * mm, "end": v(45.82, -19.72) * mm});
            skLineSegment(sketch, "E111.4.0.108", {"start": v(36.92, -37.1) * mm, "end": v(35.84, -35.7) * mm});
            skLineSegment(sketch, "E111.4.0.109", {"start": v(37.58, 36) * mm, "end": v(36.95, 35.1) * mm});
            skLineSegment(sketch, "E111.4.0.110", {"start": v(34.5, 19.65) * mm, "end": v(34.5, 11.85) * mm});
            skArc(sketch, "E111.4.0.111", {"start": v(44.55, -26.25) * mm, "mid": v(44.35, -26.73) * mm, "end": v(43.87, -26.92) * mm});
            skArc(sketch, "E111.4.0.112", {"start": v(34.5, -27.6) * mm, "mid": v(34.7, -27.12) * mm, "end": v(35.17, -26.92) * mm});
            skArc(sketch, "E111.4.0.113", {"start": v(43.87, 20.32) * mm, "mid": v(44.35, 20.52) * mm, "end": v(44.55, 21) * mm});
            skLineSegment(sketch, "E111.4.0.114", {"start": v(35.77, -2.63) * mm, "end": v(35.77, 0) * mm});
            skArc(sketch, "E111.4.0.115", {"start": v(36.44, 3.3) * mm, "mid": v(35.97, 3.1) * mm, "end": v(35.77, 2.63) * mm});
            skArc(sketch, "E111.4.0.116", {"start": v(45.14, 19.05) * mm, "mid": v(45.62, 19.25) * mm, "end": v(45.82, 19.72) * mm});
            skArc(sketch, "E111.4.0.117", {"start": v(43.87, 4.57) * mm, "mid": v(44.35, 4.77) * mm, "end": v(44.55, 5.24) * mm});
            skArc(sketch, "E111.4.0.118", {"start": v(45.14, 3.3) * mm, "mid": v(45.62, 3.5) * mm, "end": v(45.82, 3.97) * mm});
            skArc(sketch, "E111.4.0.119", {"start": v(45.82, 11.77) * mm, "mid": v(45.62, 12.25) * mm, "end": v(45.14, 12.45) * mm});
            skLineSegment(sketch, "E111.4.0.120", {"start": v(35.77, -31.43) * mm, "end": v(35.77, -30.73) * mm});
            skLineSegment(sketch, "E111.4.0.121", {"start": v(34.5, -3.9) * mm, "end": v(34.5, 0) * mm});
            skArc(sketch, "E111.4.0.122", {"start": v(45.82, 27.52) * mm, "mid": v(45.62, 28) * mm, "end": v(45.14, 28.2) * mm});
            skArc(sketch, "E111.4.0.123", {"start": v(44.55, 26.25) * mm, "mid": v(44.35, 26.73) * mm, "end": v(43.87, 26.92) * mm});
            skArc(sketch, "E111.4.0.124", {"start": v(35.17, -4.57) * mm, "mid": v(34.7, -4.38) * mm, "end": v(34.5, -3.9) * mm});
            skArc(sketch, "E111.4.0.125", {"start": v(36.44, -3.3) * mm, "mid": v(35.97, -3.1) * mm, "end": v(35.77, -2.63) * mm});
            skArc(sketch, "E111.4.0.126", {"start": v(34.5, 11.85) * mm, "mid": v(34.7, 11.37) * mm, "end": v(35.17, 11.18) * mm});
            skArc(sketch, "E111.4.0.127", {"start": v(35.17, 4.57) * mm, "mid": v(34.7, 4.38) * mm, "end": v(34.5, 3.9) * mm});
            skArc(sketch, "E111.4.0.128", {"start": v(34.5, 27.6) * mm, "mid": v(34.7, 27.12) * mm, "end": v(35.17, 26.92) * mm});
            skLineSegment(sketch, "E111.4.0.129", {"start": v(35.77, 2.63) * mm, "end": v(35.77, 0) * mm});
            skArc(sketch, "E111.4.0.130", {"start": v(44.55, 10.5) * mm, "mid": v(44.35, 10.98) * mm, "end": v(43.87, 11.18) * mm});
            skLineSegment(sketch, "E111.4.0.131", {"start": v(34.5, 3.9) * mm, "end": v(34.5, 0) * mm});
            skPoint(sketch, "E111.5.0.0", {"position": v(48.47, 33.45) * mm});
            skPoint(sketch, "E111.5.0.1", {"position": v(58.52, 19.05) * mm});
            skPoint(sketch, "E111.5.0.2", {"position": v(47.2, -26.92) * mm});
            skLineSegment(sketch, "E111.5.0.3", {"start": v(48.47, -12.45) * mm, "end": v(57.84, -12.45) * mm});
            skLineSegment(sketch, "E111.5.0.4", {"start": v(56.57, -20.32) * mm, "end": v(47.87, -20.32) * mm});
            skPoint(sketch, "E111.5.0.5", {"position": v(47.2, -33.98) * mm});
            skPoint(sketch, "E111.5.0.6", {"position": v(50.55, 38.29) * mm});
            skPoint(sketch, "E111.5.0.7", {"position": v(51.24, -37.35) * mm});
            skPoint(sketch, "E111.5.0.8", {"position": v(47.2, -11.18) * mm});
            skLineSegment(sketch, "E111.5.0.9", {"start": v(57.84, -3.3) * mm, "end": v(49.14, -3.3) * mm});
            skPoint(sketch, "E111.5.0.10", {"position": v(47.2, 20.32) * mm});
            skPoint(sketch, "E111.5.0.11", {"position": v(47.2, -20.32) * mm});
            skPoint(sketch, "E111.5.0.12", {"position": v(47.2, 33.98) * mm});
            skPoint(sketch, "E111.5.0.13", {"position": v(58.52, -3.3) * mm});
            skPoint(sketch, "E111.5.0.14", {"position": v(57.25, -11.18) * mm});
            skPoint(sketch, "E111.5.0.15", {"position": v(58.52, -12.45) * mm});
            skLineSegment(sketch, "E111.5.0.16", {"start": v(56.57, -4.57) * mm, "end": v(47.87, -4.57) * mm});
            skPoint(sketch, "E111.5.0.17", {"position": v(63.5, -43.18) * mm});
            skPoint(sketch, "E111.5.0.18", {"position": v(58.52, -19.05) * mm});
            skPoint(sketch, "E111.5.0.19", {"position": v(63.5, 43.18) * mm});
            skPoint(sketch, "E111.5.0.20", {"position": v(58.52, -28.2) * mm});
            skPoint(sketch, "E111.5.0.21", {"position": v(47.2, 26.92) * mm});
            skPoint(sketch, "E111.5.0.22", {"position": v(51.24, 37.35) * mm});
            skPoint(sketch, "E111.5.0.23", {"position": v(48.47, -33.45) * mm});
            skLineSegment(sketch, "E111.5.0.24", {"start": v(63.5, 44.45) * mm, "end": v(51.91, 38.94) * mm});
            skPoint(sketch, "E111.5.0.25", {"position": v(57.25, -20.32) * mm});
            skPoint(sketch, "E111.5.0.26", {"position": v(48.47, -3.3) * mm});
            skPoint(sketch, "E111.5.0.27", {"position": v(57.25, -26.92) * mm});
            skLineSegment(sketch, "E111.5.0.28", {"start": v(57.84, -19.05) * mm, "end": v(49.14, -19.05) * mm});
            skLineSegment(sketch, "E111.5.0.29", {"start": v(62.2, -42.56) * mm, "end": v(52.73, -38.06) * mm});
            skPoint(sketch, "E111.5.0.30", {"position": v(47.2, -4.57) * mm});
            skPoint(sketch, "E111.5.0.31", {"position": v(48.47, -28.2) * mm});
            skLineSegment(sketch, "E111.5.0.32", {"start": v(63.5, -44.45) * mm, "end": v(51.91, -38.94) * mm});
            skLineSegment(sketch, "E111.5.0.33", {"start": v(62.2, 42.56) * mm, "end": v(52.73, 38.06) * mm});
            skPoint(sketch, "E111.5.0.34", {"position": v(57.25, -4.57) * mm});
            skPoint(sketch, "E111.5.0.35", {"position": v(50.55, -38.29) * mm});
            skLineSegment(sketch, "E111.5.0.36", {"start": v(47.87, -11.18) * mm, "end": v(56.57, -11.18) * mm});
            skPoint(sketch, "E111.5.0.37", {"position": v(48.47, -19.05) * mm});
            skPoint(sketch, "E111.5.0.38", {"position": v(57.25, 4.57) * mm});
            skPoint(sketch, "E111.5.0.39", {"position": v(57.25, 26.92) * mm});
            skPoint(sketch, "E111.5.0.40", {"position": v(57.25, 11.18) * mm});
            skLineSegment(sketch, "E111.5.0.41", {"start": v(57.84, 19.05) * mm, "end": v(49.14, 19.05) * mm});
            skPoint(sketch, "E111.5.0.42", {"position": v(63.5, 43.18) * mm});
            skPoint(sketch, "E111.5.0.43", {"position": v(63.5, -43.18) * mm});
            skPoint(sketch, "E111.5.0.44", {"position": v(47.2, 11.18) * mm});
            skPoint(sketch, "E111.5.0.45", {"position": v(47.2, 4.57) * mm});
            skLineSegment(sketch, "E111.5.0.46", {"start": v(57.84, 3.3) * mm, "end": v(49.14, 3.3) * mm});
            skLineSegment(sketch, "E111.5.0.47", {"start": v(56.57, 4.57) * mm, "end": v(47.87, 4.57) * mm});
            skPoint(sketch, "E111.5.0.48", {"position": v(57.25, 20.32) * mm});
            skPoint(sketch, "E111.5.0.49", {"position": v(48.47, 19.05) * mm});
            skPoint(sketch, "E111.5.0.50", {"position": v(48.47, 28.2) * mm});
            skPoint(sketch, "E111.5.0.51", {"position": v(48.47, 3.3) * mm});
            skLineSegment(sketch, "E111.5.0.52", {"start": v(56.57, 20.32) * mm, "end": v(47.87, 20.32) * mm});
            skLineSegment(sketch, "E111.5.0.53", {"start": v(48.47, 12.45) * mm, "end": v(57.84, 12.45) * mm});
            skPoint(sketch, "E111.5.0.54", {"position": v(58.52, 28.2) * mm});
            skLineSegment(sketch, "E111.5.0.55", {"start": v(47.87, 11.18) * mm, "end": v(56.57, 11.18) * mm});
            skPoint(sketch, "E111.5.0.56", {"position": v(58.52, 12.45) * mm});
            skPoint(sketch, "E111.5.0.57", {"position": v(58.52, 3.3) * mm});
            skLineSegment(sketch, "E111.5.0.58", {"start": v(67.3, -43.18) * mm, "end": v(64.93, -43.18) * mm});
            skLineSegment(sketch, "E111.5.0.59", {"start": v(63.5, -44.45) * mm, "end": v(67.3, -44.45) * mm});
            skLineSegment(sketch, "E111.5.0.60", {"start": v(47.87, -26.92) * mm, "end": v(56.57, -26.92) * mm});
            skLineSegment(sketch, "E111.5.0.61", {"start": v(67.3, 43.18) * mm, "end": v(64.93, 43.18) * mm});
            skLineSegment(sketch, "E111.5.0.62", {"start": v(67.3, 44.45) * mm, "end": v(67.3, 43.18) * mm});
            skLineSegment(sketch, "E111.5.0.63", {"start": v(58.52, -27.52) * mm, "end": v(58.52, -19.72) * mm});
            skArc(sketch, "E111.5.0.64", {"start": v(52.73, 38.06) * mm, "mid": v(51.37, 37.19) * mm, "end": v(50.28, 36) * mm});
            skLineSegment(sketch, "E111.5.0.65", {"start": v(67.3, -44.45) * mm, "end": v(67.3, -43.18) * mm});
            skLineSegment(sketch, "E111.5.0.66", {"start": v(57.25, -10.5) * mm, "end": v(57.25, -5.24) * mm});
            skArc(sketch, "E111.5.0.67", {"start": v(51.91, -38.94) * mm, "mid": v(50.66, -38.15) * mm, "end": v(49.62, -37.1) * mm});
            skLineSegment(sketch, "E111.5.0.68", {"start": v(47.2, -19.65) * mm, "end": v(47.2, -11.85) * mm});
            skLineSegment(sketch, "E111.5.0.69", {"start": v(51.01, -28.2) * mm, "end": v(57.84, -28.2) * mm});
            skLineSegment(sketch, "E111.5.0.70", {"start": v(57.25, -26.25) * mm, "end": v(57.25, -21) * mm});
            skLineSegment(sketch, "E111.5.0.71", {"start": v(51.01, 28.2) * mm, "end": v(57.84, 28.2) * mm});
            skLineSegment(sketch, "E111.5.0.72", {"start": v(58.52, -11.77) * mm, "end": v(58.52, -3.97) * mm});
            skLineSegment(sketch, "E111.5.0.73", {"start": v(63.5, 44.45) * mm, "end": v(67.3, 44.45) * mm});
            skLineSegment(sketch, "E111.5.0.74", {"start": v(48.47, -18.38) * mm, "end": v(48.47, -12.45) * mm});
            skArc(sketch, "E111.5.0.75", {"start": v(52.73, -38.06) * mm, "mid": v(51.37, -37.19) * mm, "end": v(50.28, -36) * mm});
            skLineSegment(sketch, "E111.5.0.76", {"start": v(47.87, 26.92) * mm, "end": v(56.57, 26.92) * mm});
            skArc(sketch, "E111.5.0.77", {"start": v(48.54, 35.7) * mm, "mid": v(47.54, 33.86) * mm, "end": v(47.2, 31.8) * mm});
            skArc(sketch, "E111.5.0.78", {"start": v(58.52, -27.52) * mm, "mid": v(58.32, -28) * mm, "end": v(57.84, -28.2) * mm});
            skLineSegment(sketch, "E111.5.0.79", {"start": v(58.52, 27.52) * mm, "end": v(58.52, 19.72) * mm});
            skArc(sketch, "E111.5.0.80", {"start": v(56.57, -4.57) * mm, "mid": v(57.05, -4.77) * mm, "end": v(57.25, -5.24) * mm});
            skArc(sketch, "E111.5.0.81", {"start": v(48.54, -35.7) * mm, "mid": v(47.54, -33.86) * mm, "end": v(47.2, -31.8) * mm});
            skArc(sketch, "E111.5.0.82", {"start": v(47.87, -20.32) * mm, "mid": v(47.4, -20.12) * mm, "end": v(47.2, -19.65) * mm});
            skArc(sketch, "E111.5.0.83", {"start": v(57.84, -3.3) * mm, "mid": v(58.32, -3.5) * mm, "end": v(58.52, -3.97) * mm});
            skArc(sketch, "E111.5.0.84", {"start": v(49.65, 35.1) * mm, "mid": v(48.77, 33.36) * mm, "end": v(48.47, 31.43) * mm});
            skLineSegment(sketch, "E111.5.0.85", {"start": v(48.47, 18.38) * mm, "end": v(48.47, 12.45) * mm});
            skArc(sketch, "E111.5.0.86", {"start": v(49.65, -35.1) * mm, "mid": v(48.77, -33.36) * mm, "end": v(48.47, -31.43) * mm});
            skArc(sketch, "E111.5.0.87", {"start": v(48.47, -30.73) * mm, "mid": v(49.21, -28.94) * mm, "end": v(51.01, -28.2) * mm});
            skArc(sketch, "E111.5.0.88", {"start": v(57.25, -10.5) * mm, "mid": v(57.05, -10.98) * mm, "end": v(56.57, -11.18) * mm});
            skArc(sketch, "E111.5.0.89", {"start": v(47.87, 20.32) * mm, "mid": v(47.4, 20.12) * mm, "end": v(47.2, 19.65) * mm});
            skArc(sketch, "E111.5.0.90", {"start": v(51.91, 38.94) * mm, "mid": v(50.66, 38.15) * mm, "end": v(49.62, 37.1) * mm});
            skLineSegment(sketch, "E111.5.0.91", {"start": v(57.25, 10.5) * mm, "end": v(57.25, 5.24) * mm});
            skArc(sketch, "E111.5.0.92", {"start": v(48.47, 30.73) * mm, "mid": v(49.21, 28.94) * mm, "end": v(51.01, 28.2) * mm});
            skArc(sketch, "E111.5.0.93", {"start": v(64.93, 43.18) * mm, "mid": v(63.54, 43.02) * mm, "end": v(62.2, 42.56) * mm});
            skLineSegment(sketch, "E111.5.0.94", {"start": v(50.28, -36) * mm, "end": v(49.65, -35.1) * mm});
            skArc(sketch, "E111.5.0.95", {"start": v(49.14, -19.05) * mm, "mid": v(48.67, -18.85) * mm, "end": v(48.47, -18.38) * mm});
            skArc(sketch, "E111.5.0.96", {"start": v(49.14, 19.05) * mm, "mid": v(48.67, 18.85) * mm, "end": v(48.47, 18.38) * mm});
            skLineSegment(sketch, "E111.5.0.97", {"start": v(47.2, -31.8) * mm, "end": v(47.2, -27.6) * mm});
            skArc(sketch, "E111.5.0.98", {"start": v(58.52, -11.77) * mm, "mid": v(58.32, -12.25) * mm, "end": v(57.84, -12.45) * mm});
            skLineSegment(sketch, "E111.5.0.99", {"start": v(58.52, 11.77) * mm, "end": v(58.52, 3.97) * mm});
            skLineSegment(sketch, "E111.5.0.100", {"start": v(48.47, 31.43) * mm, "end": v(48.47, 30.73) * mm});
            skLineSegment(sketch, "E111.5.0.101", {"start": v(57.25, 26.25) * mm, "end": v(57.25, 21) * mm});
            skArc(sketch, "E111.5.0.102", {"start": v(56.57, -20.32) * mm, "mid": v(57.05, -20.52) * mm, "end": v(57.25, -21) * mm});
            skArc(sketch, "E111.5.0.103", {"start": v(47.2, -11.85) * mm, "mid": v(47.4, -11.37) * mm, "end": v(47.87, -11.18) * mm});
            skLineSegment(sketch, "E111.5.0.104", {"start": v(49.62, 37.1) * mm, "end": v(48.54, 35.7) * mm});
            skLineSegment(sketch, "E111.5.0.105", {"start": v(47.2, 31.8) * mm, "end": v(47.2, 27.6) * mm});
            skArc(sketch, "E111.5.0.106", {"start": v(64.93, -43.18) * mm, "mid": v(63.54, -43.02) * mm, "end": v(62.2, -42.56) * mm});
            skArc(sketch, "E111.5.0.107", {"start": v(57.84, -19.05) * mm, "mid": v(58.32, -19.25) * mm, "end": v(58.52, -19.72) * mm});
            skLineSegment(sketch, "E111.5.0.108", {"start": v(49.62, -37.1) * mm, "end": v(48.54, -35.7) * mm});
            skLineSegment(sketch, "E111.5.0.109", {"start": v(50.28, 36) * mm, "end": v(49.65, 35.1) * mm});
            skLineSegment(sketch, "E111.5.0.110", {"start": v(47.2, 19.65) * mm, "end": v(47.2, 11.85) * mm});
            skArc(sketch, "E111.5.0.111", {"start": v(57.25, -26.25) * mm, "mid": v(57.05, -26.73) * mm, "end": v(56.57, -26.92) * mm});
            skArc(sketch, "E111.5.0.112", {"start": v(47.2, -27.6) * mm, "mid": v(47.4, -27.12) * mm, "end": v(47.87, -26.92) * mm});
            skArc(sketch, "E111.5.0.113", {"start": v(56.57, 20.32) * mm, "mid": v(57.05, 20.52) * mm, "end": v(57.25, 21) * mm});
            skLineSegment(sketch, "E111.5.0.114", {"start": v(48.47, -2.63) * mm, "end": v(48.47, 0) * mm});
            skArc(sketch, "E111.5.0.115", {"start": v(49.14, 3.3) * mm, "mid": v(48.67, 3.1) * mm, "end": v(48.47, 2.63) * mm});
            skArc(sketch, "E111.5.0.116", {"start": v(57.84, 19.05) * mm, "mid": v(58.32, 19.25) * mm, "end": v(58.52, 19.72) * mm});
            skArc(sketch, "E111.5.0.117", {"start": v(56.57, 4.57) * mm, "mid": v(57.05, 4.77) * mm, "end": v(57.25, 5.24) * mm});
            skArc(sketch, "E111.5.0.118", {"start": v(57.84, 3.3) * mm, "mid": v(58.32, 3.5) * mm, "end": v(58.52, 3.97) * mm});
            skArc(sketch, "E111.5.0.119", {"start": v(58.52, 11.77) * mm, "mid": v(58.32, 12.25) * mm, "end": v(57.84, 12.45) * mm});
            skLineSegment(sketch, "E111.5.0.120", {"start": v(48.47, -31.43) * mm, "end": v(48.47, -30.73) * mm});
            skLineSegment(sketch, "E111.5.0.121", {"start": v(47.2, -3.9) * mm, "end": v(47.2, 0) * mm});
            skArc(sketch, "E111.5.0.122", {"start": v(58.52, 27.52) * mm, "mid": v(58.32, 28) * mm, "end": v(57.84, 28.2) * mm});
            skArc(sketch, "E111.5.0.123", {"start": v(57.25, 26.25) * mm, "mid": v(57.05, 26.73) * mm, "end": v(56.57, 26.92) * mm});
            skArc(sketch, "E111.5.0.124", {"start": v(47.87, -4.57) * mm, "mid": v(47.4, -4.38) * mm, "end": v(47.2, -3.9) * mm});
            skArc(sketch, "E111.5.0.125", {"start": v(49.14, -3.3) * mm, "mid": v(48.67, -3.1) * mm, "end": v(48.47, -2.63) * mm});
            skArc(sketch, "E111.5.0.126", {"start": v(47.2, 11.85) * mm, "mid": v(47.4, 11.37) * mm, "end": v(47.87, 11.18) * mm});
            skArc(sketch, "E111.5.0.127", {"start": v(47.87, 4.57) * mm, "mid": v(47.4, 4.38) * mm, "end": v(47.2, 3.9) * mm});
            skArc(sketch, "E111.5.0.128", {"start": v(47.2, 27.6) * mm, "mid": v(47.4, 27.12) * mm, "end": v(47.87, 26.92) * mm});
            skLineSegment(sketch, "E111.5.0.129", {"start": v(48.47, 2.63) * mm, "end": v(48.47, 0) * mm});
            skArc(sketch, "E111.5.0.130", {"start": v(57.25, 10.5) * mm, "mid": v(57.05, 10.98) * mm, "end": v(56.57, 11.18) * mm});
            skLineSegment(sketch, "E111.5.0.131", {"start": v(47.2, 3.9) * mm, "end": v(47.2, 0) * mm});
            skPoint(sketch, "E111.6.0.0", {"position": v(61.17, 33.45) * mm});
            skPoint(sketch, "E111.6.0.1", {"position": v(71.22, 19.05) * mm});
            skPoint(sketch, "E111.6.0.2", {"position": v(59.9, -26.92) * mm});
            skLineSegment(sketch, "E111.6.0.3", {"start": v(61.17, -12.45) * mm, "end": v(70.54, -12.45) * mm});
            skLineSegment(sketch, "E111.6.0.4", {"start": v(69.27, -20.32) * mm, "end": v(60.57, -20.32) * mm});
            skPoint(sketch, "E111.6.0.5", {"position": v(59.9, -33.98) * mm});
            skPoint(sketch, "E111.6.0.6", {"position": v(63.25, 38.29) * mm});
            skPoint(sketch, "E111.6.0.7", {"position": v(63.94, -37.35) * mm});
            skPoint(sketch, "E111.6.0.8", {"position": v(59.9, -11.18) * mm});
            skLineSegment(sketch, "E111.6.0.9", {"start": v(70.54, -3.3) * mm, "end": v(61.84, -3.3) * mm});
            skPoint(sketch, "E111.6.0.10", {"position": v(59.9, 20.32) * mm});
            skPoint(sketch, "E111.6.0.11", {"position": v(59.9, -20.32) * mm});
            skPoint(sketch, "E111.6.0.12", {"position": v(59.9, 33.98) * mm});
            skPoint(sketch, "E111.6.0.13", {"position": v(71.22, -3.3) * mm});
            skPoint(sketch, "E111.6.0.14", {"position": v(69.95, -11.18) * mm});
            skPoint(sketch, "E111.6.0.15", {"position": v(71.22, -12.45) * mm});
            skLineSegment(sketch, "E111.6.0.16", {"start": v(69.27, -4.57) * mm, "end": v(60.57, -4.57) * mm});
            skPoint(sketch, "E111.6.0.17", {"position": v(76.2, -43.18) * mm});
            skPoint(sketch, "E111.6.0.18", {"position": v(71.22, -19.05) * mm});
            skPoint(sketch, "E111.6.0.19", {"position": v(76.2, 43.18) * mm});
            skPoint(sketch, "E111.6.0.20", {"position": v(71.22, -28.2) * mm});
            skPoint(sketch, "E111.6.0.21", {"position": v(59.9, 26.92) * mm});
            skPoint(sketch, "E111.6.0.22", {"position": v(63.94, 37.35) * mm});
            skPoint(sketch, "E111.6.0.23", {"position": v(61.17, -33.45) * mm});
            skLineSegment(sketch, "E111.6.0.24", {"start": v(76.2, 44.45) * mm, "end": v(64.61, 38.94) * mm});
            skPoint(sketch, "E111.6.0.25", {"position": v(69.95, -20.32) * mm});
            skPoint(sketch, "E111.6.0.26", {"position": v(61.17, -3.3) * mm});
            skPoint(sketch, "E111.6.0.27", {"position": v(69.95, -26.92) * mm});
            skLineSegment(sketch, "E111.6.0.28", {"start": v(70.54, -19.05) * mm, "end": v(61.84, -19.05) * mm});
            skLineSegment(sketch, "E111.6.0.29", {"start": v(74.9, -42.56) * mm, "end": v(65.43, -38.06) * mm});
            skPoint(sketch, "E111.6.0.30", {"position": v(59.9, -4.57) * mm});
            skPoint(sketch, "E111.6.0.31", {"position": v(61.17, -28.2) * mm});
            skLineSegment(sketch, "E111.6.0.32", {"start": v(76.2, -44.45) * mm, "end": v(64.61, -38.94) * mm});
            skLineSegment(sketch, "E111.6.0.33", {"start": v(74.9, 42.56) * mm, "end": v(65.43, 38.06) * mm});
            skPoint(sketch, "E111.6.0.34", {"position": v(69.95, -4.57) * mm});
            skPoint(sketch, "E111.6.0.35", {"position": v(63.25, -38.29) * mm});
            skLineSegment(sketch, "E111.6.0.36", {"start": v(60.57, -11.18) * mm, "end": v(69.27, -11.18) * mm});
            skPoint(sketch, "E111.6.0.37", {"position": v(61.17, -19.05) * mm});
            skPoint(sketch, "E111.6.0.38", {"position": v(69.95, 4.57) * mm});
            skPoint(sketch, "E111.6.0.39", {"position": v(69.95, 26.92) * mm});
            skPoint(sketch, "E111.6.0.40", {"position": v(69.95, 11.18) * mm});
            skLineSegment(sketch, "E111.6.0.41", {"start": v(70.54, 19.05) * mm, "end": v(61.84, 19.05) * mm});
            skPoint(sketch, "E111.6.0.42", {"position": v(76.2, 43.18) * mm});
            skPoint(sketch, "E111.6.0.43", {"position": v(76.2, -43.18) * mm});
            skPoint(sketch, "E111.6.0.44", {"position": v(59.9, 11.18) * mm});
            skPoint(sketch, "E111.6.0.45", {"position": v(59.9, 4.57) * mm});
            skLineSegment(sketch, "E111.6.0.46", {"start": v(70.54, 3.3) * mm, "end": v(61.84, 3.3) * mm});
            skLineSegment(sketch, "E111.6.0.47", {"start": v(69.27, 4.57) * mm, "end": v(60.57, 4.57) * mm});
            skPoint(sketch, "E111.6.0.48", {"position": v(69.95, 20.32) * mm});
            skPoint(sketch, "E111.6.0.49", {"position": v(61.17, 19.05) * mm});
            skPoint(sketch, "E111.6.0.50", {"position": v(61.17, 28.2) * mm});
            skPoint(sketch, "E111.6.0.51", {"position": v(61.17, 3.3) * mm});
            skLineSegment(sketch, "E111.6.0.52", {"start": v(69.27, 20.32) * mm, "end": v(60.57, 20.32) * mm});
            skLineSegment(sketch, "E111.6.0.53", {"start": v(61.17, 12.45) * mm, "end": v(70.54, 12.45) * mm});
            skPoint(sketch, "E111.6.0.54", {"position": v(71.22, 28.2) * mm});
            skLineSegment(sketch, "E111.6.0.55", {"start": v(60.57, 11.18) * mm, "end": v(69.27, 11.18) * mm});
            skPoint(sketch, "E111.6.0.56", {"position": v(71.22, 12.45) * mm});
            skPoint(sketch, "E111.6.0.57", {"position": v(71.22, 3.3) * mm});
            skLineSegment(sketch, "E111.6.0.58", {"start": v(80, -43.18) * mm, "end": v(77.63, -43.18) * mm});
            skLineSegment(sketch, "E111.6.0.59", {"start": v(76.2, -44.45) * mm, "end": v(80, -44.45) * mm});
            skLineSegment(sketch, "E111.6.0.60", {"start": v(60.57, -26.92) * mm, "end": v(69.27, -26.92) * mm});
            skLineSegment(sketch, "E111.6.0.61", {"start": v(80, 43.18) * mm, "end": v(77.63, 43.18) * mm});
            skLineSegment(sketch, "E111.6.0.62", {"start": v(80, 44.45) * mm, "end": v(80, 43.18) * mm});
            skLineSegment(sketch, "E111.6.0.63", {"start": v(71.22, -27.52) * mm, "end": v(71.22, -19.72) * mm});
            skArc(sketch, "E111.6.0.64", {"start": v(65.43, 38.06) * mm, "mid": v(64.07, 37.19) * mm, "end": v(62.98, 36) * mm});
            skLineSegment(sketch, "E111.6.0.65", {"start": v(80, -44.45) * mm, "end": v(80, -43.18) * mm});
            skLineSegment(sketch, "E111.6.0.66", {"start": v(69.95, -10.5) * mm, "end": v(69.95, -5.24) * mm});
            skArc(sketch, "E111.6.0.67", {"start": v(64.61, -38.94) * mm, "mid": v(63.36, -38.15) * mm, "end": v(62.32, -37.1) * mm});
            skLineSegment(sketch, "E111.6.0.68", {"start": v(59.9, -19.65) * mm, "end": v(59.9, -11.85) * mm});
            skLineSegment(sketch, "E111.6.0.69", {"start": v(63.71, -28.2) * mm, "end": v(70.54, -28.2) * mm});
            skLineSegment(sketch, "E111.6.0.70", {"start": v(69.95, -26.25) * mm, "end": v(69.95, -21) * mm});
            skLineSegment(sketch, "E111.6.0.71", {"start": v(63.71, 28.2) * mm, "end": v(70.54, 28.2) * mm});
            skLineSegment(sketch, "E111.6.0.72", {"start": v(71.22, -11.77) * mm, "end": v(71.22, -3.97) * mm});
            skLineSegment(sketch, "E111.6.0.73", {"start": v(76.2, 44.45) * mm, "end": v(80, 44.45) * mm});
            skLineSegment(sketch, "E111.6.0.74", {"start": v(61.17, -18.38) * mm, "end": v(61.17, -12.45) * mm});
            skArc(sketch, "E111.6.0.75", {"start": v(65.43, -38.06) * mm, "mid": v(64.07, -37.19) * mm, "end": v(62.98, -36) * mm});
            skLineSegment(sketch, "E111.6.0.76", {"start": v(60.57, 26.92) * mm, "end": v(69.27, 26.92) * mm});
            skArc(sketch, "E111.6.0.77", {"start": v(61.24, 35.7) * mm, "mid": v(60.24, 33.86) * mm, "end": v(59.9, 31.8) * mm});
            skArc(sketch, "E111.6.0.78", {"start": v(71.22, -27.52) * mm, "mid": v(71.02, -28) * mm, "end": v(70.54, -28.2) * mm});
            skLineSegment(sketch, "E111.6.0.79", {"start": v(71.22, 27.52) * mm, "end": v(71.22, 19.72) * mm});
            skArc(sketch, "E111.6.0.80", {"start": v(69.27, -4.57) * mm, "mid": v(69.75, -4.77) * mm, "end": v(69.95, -5.24) * mm});
            skArc(sketch, "E111.6.0.81", {"start": v(61.24, -35.7) * mm, "mid": v(60.24, -33.86) * mm, "end": v(59.9, -31.8) * mm});
            skArc(sketch, "E111.6.0.82", {"start": v(60.57, -20.32) * mm, "mid": v(60.1, -20.12) * mm, "end": v(59.9, -19.65) * mm});
            skArc(sketch, "E111.6.0.83", {"start": v(70.54, -3.3) * mm, "mid": v(71.02, -3.5) * mm, "end": v(71.22, -3.97) * mm});
            skArc(sketch, "E111.6.0.84", {"start": v(62.35, 35.1) * mm, "mid": v(61.47, 33.36) * mm, "end": v(61.17, 31.43) * mm});
            skLineSegment(sketch, "E111.6.0.85", {"start": v(61.17, 18.38) * mm, "end": v(61.17, 12.45) * mm});
            skArc(sketch, "E111.6.0.86", {"start": v(62.35, -35.1) * mm, "mid": v(61.47, -33.36) * mm, "end": v(61.17, -31.43) * mm});
            skArc(sketch, "E111.6.0.87", {"start": v(61.17, -30.73) * mm, "mid": v(61.91, -28.94) * mm, "end": v(63.71, -28.2) * mm});
            skArc(sketch, "E111.6.0.88", {"start": v(69.95, -10.5) * mm, "mid": v(69.75, -10.98) * mm, "end": v(69.27, -11.18) * mm});
            skArc(sketch, "E111.6.0.89", {"start": v(60.57, 20.32) * mm, "mid": v(60.1, 20.12) * mm, "end": v(59.9, 19.65) * mm});
            skArc(sketch, "E111.6.0.90", {"start": v(64.61, 38.94) * mm, "mid": v(63.36, 38.15) * mm, "end": v(62.32, 37.1) * mm});
            skLineSegment(sketch, "E111.6.0.91", {"start": v(69.95, 10.5) * mm, "end": v(69.95, 5.24) * mm});
            skArc(sketch, "E111.6.0.92", {"start": v(61.17, 30.73) * mm, "mid": v(61.91, 28.94) * mm, "end": v(63.71, 28.2) * mm});
            skArc(sketch, "E111.6.0.93", {"start": v(77.63, 43.18) * mm, "mid": v(76.24, 43.02) * mm, "end": v(74.9, 42.56) * mm});
            skLineSegment(sketch, "E111.6.0.94", {"start": v(62.98, -36) * mm, "end": v(62.35, -35.1) * mm});
            skArc(sketch, "E111.6.0.95", {"start": v(61.84, -19.05) * mm, "mid": v(61.37, -18.85) * mm, "end": v(61.17, -18.38) * mm});
            skArc(sketch, "E111.6.0.96", {"start": v(61.84, 19.05) * mm, "mid": v(61.37, 18.85) * mm, "end": v(61.17, 18.38) * mm});
            skLineSegment(sketch, "E111.6.0.97", {"start": v(59.9, -31.8) * mm, "end": v(59.9, -27.6) * mm});
            skArc(sketch, "E111.6.0.98", {"start": v(71.22, -11.77) * mm, "mid": v(71.02, -12.25) * mm, "end": v(70.54, -12.45) * mm});
            skLineSegment(sketch, "E111.6.0.99", {"start": v(71.22, 11.77) * mm, "end": v(71.22, 3.97) * mm});
            skLineSegment(sketch, "E111.6.0.100", {"start": v(61.17, 31.43) * mm, "end": v(61.17, 30.73) * mm});
            skLineSegment(sketch, "E111.6.0.101", {"start": v(69.95, 26.25) * mm, "end": v(69.95, 21) * mm});
            skArc(sketch, "E111.6.0.102", {"start": v(69.27, -20.32) * mm, "mid": v(69.75, -20.52) * mm, "end": v(69.95, -21) * mm});
            skArc(sketch, "E111.6.0.103", {"start": v(59.9, -11.85) * mm, "mid": v(60.1, -11.37) * mm, "end": v(60.57, -11.18) * mm});
            skLineSegment(sketch, "E111.6.0.104", {"start": v(62.32, 37.1) * mm, "end": v(61.24, 35.7) * mm});
            skLineSegment(sketch, "E111.6.0.105", {"start": v(59.9, 31.8) * mm, "end": v(59.9, 27.6) * mm});
            skArc(sketch, "E111.6.0.106", {"start": v(77.63, -43.18) * mm, "mid": v(76.24, -43.02) * mm, "end": v(74.9, -42.56) * mm});
            skArc(sketch, "E111.6.0.107", {"start": v(70.54, -19.05) * mm, "mid": v(71.02, -19.25) * mm, "end": v(71.22, -19.72) * mm});
            skLineSegment(sketch, "E111.6.0.108", {"start": v(62.32, -37.1) * mm, "end": v(61.24, -35.7) * mm});
            skLineSegment(sketch, "E111.6.0.109", {"start": v(62.98, 36) * mm, "end": v(62.35, 35.1) * mm});
            skLineSegment(sketch, "E111.6.0.110", {"start": v(59.9, 19.65) * mm, "end": v(59.9, 11.85) * mm});
            skArc(sketch, "E111.6.0.111", {"start": v(69.95, -26.25) * mm, "mid": v(69.75, -26.73) * mm, "end": v(69.27, -26.92) * mm});
            skArc(sketch, "E111.6.0.112", {"start": v(59.9, -27.6) * mm, "mid": v(60.1, -27.12) * mm, "end": v(60.57, -26.92) * mm});
            skArc(sketch, "E111.6.0.113", {"start": v(69.27, 20.32) * mm, "mid": v(69.75, 20.52) * mm, "end": v(69.95, 21) * mm});
            skLineSegment(sketch, "E111.6.0.114", {"start": v(61.17, -2.63) * mm, "end": v(61.17, 0) * mm});
            skArc(sketch, "E111.6.0.115", {"start": v(61.84, 3.3) * mm, "mid": v(61.37, 3.1) * mm, "end": v(61.17, 2.63) * mm});
            skArc(sketch, "E111.6.0.116", {"start": v(70.54, 19.05) * mm, "mid": v(71.02, 19.25) * mm, "end": v(71.22, 19.72) * mm});
            skArc(sketch, "E111.6.0.117", {"start": v(69.27, 4.57) * mm, "mid": v(69.75, 4.77) * mm, "end": v(69.95, 5.24) * mm});
            skArc(sketch, "E111.6.0.118", {"start": v(70.54, 3.3) * mm, "mid": v(71.02, 3.5) * mm, "end": v(71.22, 3.97) * mm});
            skArc(sketch, "E111.6.0.119", {"start": v(71.22, 11.77) * mm, "mid": v(71.02, 12.25) * mm, "end": v(70.54, 12.45) * mm});
            skLineSegment(sketch, "E111.6.0.120", {"start": v(61.17, -31.43) * mm, "end": v(61.17, -30.73) * mm});
            skLineSegment(sketch, "E111.6.0.121", {"start": v(59.9, -3.9) * mm, "end": v(59.9, 0) * mm});
            skArc(sketch, "E111.6.0.122", {"start": v(71.22, 27.52) * mm, "mid": v(71.02, 28) * mm, "end": v(70.54, 28.2) * mm});
            skArc(sketch, "E111.6.0.123", {"start": v(69.95, 26.25) * mm, "mid": v(69.75, 26.73) * mm, "end": v(69.27, 26.92) * mm});
            skArc(sketch, "E111.6.0.124", {"start": v(60.57, -4.57) * mm, "mid": v(60.1, -4.38) * mm, "end": v(59.9, -3.9) * mm});
            skArc(sketch, "E111.6.0.125", {"start": v(61.84, -3.3) * mm, "mid": v(61.37, -3.1) * mm, "end": v(61.17, -2.63) * mm});
            skArc(sketch, "E111.6.0.126", {"start": v(59.9, 11.85) * mm, "mid": v(60.1, 11.37) * mm, "end": v(60.57, 11.18) * mm});
            skArc(sketch, "E111.6.0.127", {"start": v(60.57, 4.57) * mm, "mid": v(60.1, 4.38) * mm, "end": v(59.9, 3.9) * mm});
            skArc(sketch, "E111.6.0.128", {"start": v(59.9, 27.6) * mm, "mid": v(60.1, 27.12) * mm, "end": v(60.57, 26.92) * mm});
            skLineSegment(sketch, "E111.6.0.129", {"start": v(61.17, 2.63) * mm, "end": v(61.17, 0) * mm});
            skArc(sketch, "E111.6.0.130", {"start": v(69.95, 10.5) * mm, "mid": v(69.75, 10.98) * mm, "end": v(69.27, 11.18) * mm});
            skLineSegment(sketch, "E111.6.0.131", {"start": v(59.9, 3.9) * mm, "end": v(59.9, 0) * mm});
            skPoint(sketch, "E111.7.0.0", {"position": v(73.87, 33.45) * mm});
            skPoint(sketch, "E111.7.0.1", {"position": v(83.92, 19.05) * mm});
            skPoint(sketch, "E111.7.0.2", {"position": v(72.6, -26.92) * mm});
            skLineSegment(sketch, "E111.7.0.3", {"start": v(73.87, -12.45) * mm, "end": v(83.24, -12.45) * mm});
            skLineSegment(sketch, "E111.7.0.4", {"start": v(81.97, -20.32) * mm, "end": v(73.27, -20.32) * mm});
            skPoint(sketch, "E111.7.0.5", {"position": v(72.6, -33.98) * mm});
            skPoint(sketch, "E111.7.0.6", {"position": v(75.95, 38.29) * mm});
            skPoint(sketch, "E111.7.0.7", {"position": v(76.64, -37.35) * mm});
            skPoint(sketch, "E111.7.0.8", {"position": v(72.6, -11.18) * mm});
            skLineSegment(sketch, "E111.7.0.9", {"start": v(83.24, -3.3) * mm, "end": v(74.54, -3.3) * mm});
            skPoint(sketch, "E111.7.0.10", {"position": v(72.6, 20.32) * mm});
            skPoint(sketch, "E111.7.0.11", {"position": v(72.6, -20.32) * mm});
            skPoint(sketch, "E111.7.0.12", {"position": v(72.6, 33.98) * mm});
            skPoint(sketch, "E111.7.0.13", {"position": v(83.92, -3.3) * mm});
            skPoint(sketch, "E111.7.0.14", {"position": v(82.65, -11.18) * mm});
            skPoint(sketch, "E111.7.0.15", {"position": v(83.92, -12.45) * mm});
            skLineSegment(sketch, "E111.7.0.16", {"start": v(81.97, -4.57) * mm, "end": v(73.27, -4.57) * mm});
            skPoint(sketch, "E111.7.0.17", {"position": v(88.9, -43.18) * mm});
            skPoint(sketch, "E111.7.0.18", {"position": v(83.92, -19.05) * mm});
            skPoint(sketch, "E111.7.0.19", {"position": v(88.9, 43.18) * mm});
            skPoint(sketch, "E111.7.0.20", {"position": v(83.92, -28.2) * mm});
            skPoint(sketch, "E111.7.0.21", {"position": v(72.6, 26.92) * mm});
            skPoint(sketch, "E111.7.0.22", {"position": v(76.64, 37.35) * mm});
            skPoint(sketch, "E111.7.0.23", {"position": v(73.87, -33.45) * mm});
            skLineSegment(sketch, "E111.7.0.24", {"start": v(88.9, 44.45) * mm, "end": v(77.31, 38.94) * mm});
            skPoint(sketch, "E111.7.0.25", {"position": v(82.65, -20.32) * mm});
            skPoint(sketch, "E111.7.0.26", {"position": v(73.87, -3.3) * mm});
            skPoint(sketch, "E111.7.0.27", {"position": v(82.65, -26.92) * mm});
            skLineSegment(sketch, "E111.7.0.28", {"start": v(83.24, -19.05) * mm, "end": v(74.54, -19.05) * mm});
            skLineSegment(sketch, "E111.7.0.29", {"start": v(87.6, -42.56) * mm, "end": v(78.13, -38.06) * mm});
            skPoint(sketch, "E111.7.0.30", {"position": v(72.6, -4.57) * mm});
            skPoint(sketch, "E111.7.0.31", {"position": v(73.87, -28.2) * mm});
            skLineSegment(sketch, "E111.7.0.32", {"start": v(88.9, -44.45) * mm, "end": v(77.31, -38.94) * mm});
            skLineSegment(sketch, "E111.7.0.33", {"start": v(87.6, 42.56) * mm, "end": v(78.13, 38.06) * mm});
            skPoint(sketch, "E111.7.0.34", {"position": v(82.65, -4.57) * mm});
            skPoint(sketch, "E111.7.0.35", {"position": v(75.95, -38.29) * mm});
            skLineSegment(sketch, "E111.7.0.36", {"start": v(73.27, -11.18) * mm, "end": v(81.97, -11.18) * mm});
            skPoint(sketch, "E111.7.0.37", {"position": v(73.87, -19.05) * mm});
            skPoint(sketch, "E111.7.0.38", {"position": v(82.65, 4.57) * mm});
            skPoint(sketch, "E111.7.0.39", {"position": v(82.65, 26.92) * mm});
            skPoint(sketch, "E111.7.0.40", {"position": v(82.65, 11.18) * mm});
            skLineSegment(sketch, "E111.7.0.41", {"start": v(83.24, 19.05) * mm, "end": v(74.54, 19.05) * mm});
            skPoint(sketch, "E111.7.0.42", {"position": v(88.9, 43.18) * mm});
            skPoint(sketch, "E111.7.0.43", {"position": v(88.9, -43.18) * mm});
            skPoint(sketch, "E111.7.0.44", {"position": v(72.6, 11.18) * mm});
            skPoint(sketch, "E111.7.0.45", {"position": v(72.6, 4.57) * mm});
            skLineSegment(sketch, "E111.7.0.46", {"start": v(83.24, 3.3) * mm, "end": v(74.54, 3.3) * mm});
            skLineSegment(sketch, "E111.7.0.47", {"start": v(81.97, 4.57) * mm, "end": v(73.27, 4.57) * mm});
            skPoint(sketch, "E111.7.0.48", {"position": v(82.65, 20.32) * mm});
            skPoint(sketch, "E111.7.0.49", {"position": v(73.87, 19.05) * mm});
            skPoint(sketch, "E111.7.0.50", {"position": v(73.87, 28.2) * mm});
            skPoint(sketch, "E111.7.0.51", {"position": v(73.87, 3.3) * mm});
            skLineSegment(sketch, "E111.7.0.52", {"start": v(81.97, 20.32) * mm, "end": v(73.27, 20.32) * mm});
            skLineSegment(sketch, "E111.7.0.53", {"start": v(73.87, 12.45) * mm, "end": v(83.24, 12.45) * mm});
            skPoint(sketch, "E111.7.0.54", {"position": v(83.92, 28.2) * mm});
            skLineSegment(sketch, "E111.7.0.55", {"start": v(73.27, 11.18) * mm, "end": v(81.97, 11.18) * mm});
            skPoint(sketch, "E111.7.0.56", {"position": v(83.92, 12.45) * mm});
            skPoint(sketch, "E111.7.0.57", {"position": v(83.92, 3.3) * mm});
            skLineSegment(sketch, "E111.7.0.58", {"start": v(92.7, -43.18) * mm, "end": v(90.33, -43.18) * mm});
            skLineSegment(sketch, "E111.7.0.59", {"start": v(88.9, -44.45) * mm, "end": v(92.7, -44.45) * mm});
            skLineSegment(sketch, "E111.7.0.60", {"start": v(73.27, -26.92) * mm, "end": v(81.97, -26.92) * mm});
            skLineSegment(sketch, "E111.7.0.61", {"start": v(92.7, 43.18) * mm, "end": v(90.33, 43.18) * mm});
            skLineSegment(sketch, "E111.7.0.62", {"start": v(92.7, 44.45) * mm, "end": v(92.7, 43.18) * mm});
            skLineSegment(sketch, "E111.7.0.63", {"start": v(83.92, -27.52) * mm, "end": v(83.92, -19.72) * mm});
            skArc(sketch, "E111.7.0.64", {"start": v(78.13, 38.06) * mm, "mid": v(76.77, 37.19) * mm, "end": v(75.68, 36) * mm});
            skLineSegment(sketch, "E111.7.0.65", {"start": v(92.7, -44.45) * mm, "end": v(92.7, -43.18) * mm});
            skLineSegment(sketch, "E111.7.0.66", {"start": v(82.65, -10.5) * mm, "end": v(82.65, -5.24) * mm});
            skArc(sketch, "E111.7.0.67", {"start": v(77.31, -38.94) * mm, "mid": v(76.06, -38.15) * mm, "end": v(75.02, -37.1) * mm});
            skLineSegment(sketch, "E111.7.0.68", {"start": v(72.6, -19.65) * mm, "end": v(72.6, -11.85) * mm});
            skLineSegment(sketch, "E111.7.0.69", {"start": v(76.41, -28.2) * mm, "end": v(83.24, -28.2) * mm});
            skLineSegment(sketch, "E111.7.0.70", {"start": v(82.65, -26.25) * mm, "end": v(82.65, -21) * mm});
            skLineSegment(sketch, "E111.7.0.71", {"start": v(76.41, 28.2) * mm, "end": v(83.24, 28.2) * mm});
            skLineSegment(sketch, "E111.7.0.72", {"start": v(83.92, -11.77) * mm, "end": v(83.92, -3.97) * mm});
            skLineSegment(sketch, "E111.7.0.73", {"start": v(88.9, 44.45) * mm, "end": v(92.7, 44.45) * mm});
            skLineSegment(sketch, "E111.7.0.74", {"start": v(73.87, -18.38) * mm, "end": v(73.87, -12.45) * mm});
            skArc(sketch, "E111.7.0.75", {"start": v(78.13, -38.06) * mm, "mid": v(76.77, -37.19) * mm, "end": v(75.68, -36) * mm});
            skLineSegment(sketch, "E111.7.0.76", {"start": v(73.27, 26.92) * mm, "end": v(81.97, 26.92) * mm});
            skArc(sketch, "E111.7.0.77", {"start": v(73.94, 35.7) * mm, "mid": v(72.94, 33.86) * mm, "end": v(72.6, 31.8) * mm});
            skArc(sketch, "E111.7.0.78", {"start": v(83.92, -27.52) * mm, "mid": v(83.72, -28) * mm, "end": v(83.24, -28.2) * mm});
            skLineSegment(sketch, "E111.7.0.79", {"start": v(83.92, 27.52) * mm, "end": v(83.92, 19.72) * mm});
            skArc(sketch, "E111.7.0.80", {"start": v(81.97, -4.57) * mm, "mid": v(82.45, -4.77) * mm, "end": v(82.65, -5.24) * mm});
            skArc(sketch, "E111.7.0.81", {"start": v(73.94, -35.7) * mm, "mid": v(72.94, -33.86) * mm, "end": v(72.6, -31.8) * mm});
            skArc(sketch, "E111.7.0.82", {"start": v(73.27, -20.32) * mm, "mid": v(72.8, -20.12) * mm, "end": v(72.6, -19.65) * mm});
            skArc(sketch, "E111.7.0.83", {"start": v(83.24, -3.3) * mm, "mid": v(83.72, -3.5) * mm, "end": v(83.92, -3.97) * mm});
            skArc(sketch, "E111.7.0.84", {"start": v(75.05, 35.1) * mm, "mid": v(74.17, 33.36) * mm, "end": v(73.87, 31.43) * mm});
            skLineSegment(sketch, "E111.7.0.85", {"start": v(73.87, 18.38) * mm, "end": v(73.87, 12.45) * mm});
            skArc(sketch, "E111.7.0.86", {"start": v(75.05, -35.1) * mm, "mid": v(74.17, -33.36) * mm, "end": v(73.87, -31.43) * mm});
            skArc(sketch, "E111.7.0.87", {"start": v(73.87, -30.73) * mm, "mid": v(74.61, -28.94) * mm, "end": v(76.41, -28.2) * mm});
            skArc(sketch, "E111.7.0.88", {"start": v(82.65, -10.5) * mm, "mid": v(82.45, -10.98) * mm, "end": v(81.97, -11.18) * mm});
            skArc(sketch, "E111.7.0.89", {"start": v(73.27, 20.32) * mm, "mid": v(72.8, 20.12) * mm, "end": v(72.6, 19.65) * mm});
            skArc(sketch, "E111.7.0.90", {"start": v(77.31, 38.94) * mm, "mid": v(76.06, 38.15) * mm, "end": v(75.02, 37.1) * mm});
            skLineSegment(sketch, "E111.7.0.91", {"start": v(82.65, 10.5) * mm, "end": v(82.65, 5.24) * mm});
            skArc(sketch, "E111.7.0.92", {"start": v(73.87, 30.73) * mm, "mid": v(74.61, 28.94) * mm, "end": v(76.41, 28.2) * mm});
            skArc(sketch, "E111.7.0.93", {"start": v(90.33, 43.18) * mm, "mid": v(88.94, 43.02) * mm, "end": v(87.6, 42.56) * mm});
            skLineSegment(sketch, "E111.7.0.94", {"start": v(75.68, -36) * mm, "end": v(75.05, -35.1) * mm});
            skArc(sketch, "E111.7.0.95", {"start": v(74.54, -19.05) * mm, "mid": v(74.07, -18.85) * mm, "end": v(73.87, -18.38) * mm});
            skArc(sketch, "E111.7.0.96", {"start": v(74.54, 19.05) * mm, "mid": v(74.07, 18.85) * mm, "end": v(73.87, 18.38) * mm});
            skLineSegment(sketch, "E111.7.0.97", {"start": v(72.6, -31.8) * mm, "end": v(72.6, -27.6) * mm});
            skArc(sketch, "E111.7.0.98", {"start": v(83.92, -11.77) * mm, "mid": v(83.72, -12.25) * mm, "end": v(83.24, -12.45) * mm});
            skLineSegment(sketch, "E111.7.0.99", {"start": v(83.92, 11.77) * mm, "end": v(83.92, 3.97) * mm});
            skLineSegment(sketch, "E111.7.0.100", {"start": v(73.87, 31.43) * mm, "end": v(73.87, 30.73) * mm});
            skLineSegment(sketch, "E111.7.0.101", {"start": v(82.65, 26.25) * mm, "end": v(82.65, 21) * mm});
            skArc(sketch, "E111.7.0.102", {"start": v(81.97, -20.32) * mm, "mid": v(82.45, -20.52) * mm, "end": v(82.65, -21) * mm});
            skArc(sketch, "E111.7.0.103", {"start": v(72.6, -11.85) * mm, "mid": v(72.8, -11.37) * mm, "end": v(73.27, -11.18) * mm});
            skLineSegment(sketch, "E111.7.0.104", {"start": v(75.02, 37.1) * mm, "end": v(73.94, 35.7) * mm});
            skLineSegment(sketch, "E111.7.0.105", {"start": v(72.6, 31.8) * mm, "end": v(72.6, 27.6) * mm});
            skArc(sketch, "E111.7.0.106", {"start": v(90.33, -43.18) * mm, "mid": v(88.94, -43.02) * mm, "end": v(87.6, -42.56) * mm});
            skArc(sketch, "E111.7.0.107", {"start": v(83.24, -19.05) * mm, "mid": v(83.72, -19.25) * mm, "end": v(83.92, -19.72) * mm});
            skLineSegment(sketch, "E111.7.0.108", {"start": v(75.02, -37.1) * mm, "end": v(73.94, -35.7) * mm});
            skLineSegment(sketch, "E111.7.0.109", {"start": v(75.68, 36) * mm, "end": v(75.05, 35.1) * mm});
            skLineSegment(sketch, "E111.7.0.110", {"start": v(72.6, 19.65) * mm, "end": v(72.6, 11.85) * mm});
            skArc(sketch, "E111.7.0.111", {"start": v(82.65, -26.25) * mm, "mid": v(82.45, -26.73) * mm, "end": v(81.97, -26.92) * mm});
            skArc(sketch, "E111.7.0.112", {"start": v(72.6, -27.6) * mm, "mid": v(72.8, -27.12) * mm, "end": v(73.27, -26.92) * mm});
            skArc(sketch, "E111.7.0.113", {"start": v(81.97, 20.32) * mm, "mid": v(82.45, 20.52) * mm, "end": v(82.65, 21) * mm});
            skLineSegment(sketch, "E111.7.0.114", {"start": v(73.87, -2.63) * mm, "end": v(73.87, 0) * mm});
            skArc(sketch, "E111.7.0.115", {"start": v(74.54, 3.3) * mm, "mid": v(74.07, 3.1) * mm, "end": v(73.87, 2.63) * mm});
            skArc(sketch, "E111.7.0.116", {"start": v(83.24, 19.05) * mm, "mid": v(83.72, 19.25) * mm, "end": v(83.92, 19.72) * mm});
            skArc(sketch, "E111.7.0.117", {"start": v(81.97, 4.57) * mm, "mid": v(82.45, 4.77) * mm, "end": v(82.65, 5.24) * mm});
            skArc(sketch, "E111.7.0.118", {"start": v(83.24, 3.3) * mm, "mid": v(83.72, 3.5) * mm, "end": v(83.92, 3.97) * mm});
            skArc(sketch, "E111.7.0.119", {"start": v(83.92, 11.77) * mm, "mid": v(83.72, 12.25) * mm, "end": v(83.24, 12.45) * mm});
            skLineSegment(sketch, "E111.7.0.120", {"start": v(73.87, -31.43) * mm, "end": v(73.87, -30.73) * mm});
            skLineSegment(sketch, "E111.7.0.121", {"start": v(72.6, -3.9) * mm, "end": v(72.6, 0) * mm});
            skArc(sketch, "E111.7.0.122", {"start": v(83.92, 27.52) * mm, "mid": v(83.72, 28) * mm, "end": v(83.24, 28.2) * mm});
            skArc(sketch, "E111.7.0.123", {"start": v(82.65, 26.25) * mm, "mid": v(82.45, 26.73) * mm, "end": v(81.97, 26.92) * mm});
            skArc(sketch, "E111.7.0.124", {"start": v(73.27, -4.57) * mm, "mid": v(72.8, -4.38) * mm, "end": v(72.6, -3.9) * mm});
            skArc(sketch, "E111.7.0.125", {"start": v(74.54, -3.3) * mm, "mid": v(74.07, -3.1) * mm, "end": v(73.87, -2.63) * mm});
            skArc(sketch, "E111.7.0.126", {"start": v(72.6, 11.85) * mm, "mid": v(72.8, 11.37) * mm, "end": v(73.27, 11.18) * mm});
            skArc(sketch, "E111.7.0.127", {"start": v(73.27, 4.57) * mm, "mid": v(72.8, 4.38) * mm, "end": v(72.6, 3.9) * mm});
            skArc(sketch, "E111.7.0.128", {"start": v(72.6, 27.6) * mm, "mid": v(72.8, 27.12) * mm, "end": v(73.27, 26.92) * mm});
            skLineSegment(sketch, "E111.7.0.129", {"start": v(73.87, 2.63) * mm, "end": v(73.87, 0) * mm});
            skArc(sketch, "E111.7.0.130", {"start": v(82.65, 10.5) * mm, "mid": v(82.45, 10.98) * mm, "end": v(81.97, 11.18) * mm});
            skLineSegment(sketch, "E111.7.0.131", {"start": v(72.6, 3.9) * mm, "end": v(72.6, 0) * mm});
            skPoint(sketch, "E111.8.0.0", {"position": v(86.57, 33.45) * mm});
            skPoint(sketch, "E111.8.0.1", {"position": v(96.62, 19.05) * mm});
            skPoint(sketch, "E111.8.0.2", {"position": v(85.3, -26.92) * mm});
            skLineSegment(sketch, "E111.8.0.3", {"start": v(86.57, -12.45) * mm, "end": v(95.94, -12.45) * mm});
            skLineSegment(sketch, "E111.8.0.4", {"start": v(94.67, -20.32) * mm, "end": v(85.97, -20.32) * mm});
            skPoint(sketch, "E111.8.0.5", {"position": v(85.3, -33.98) * mm});
            skPoint(sketch, "E111.8.0.6", {"position": v(88.65, 38.29) * mm});
            skPoint(sketch, "E111.8.0.7", {"position": v(89.34, -37.35) * mm});
            skPoint(sketch, "E111.8.0.8", {"position": v(85.3, -11.18) * mm});
            skLineSegment(sketch, "E111.8.0.9", {"start": v(95.94, -3.3) * mm, "end": v(87.24, -3.3) * mm});
            skPoint(sketch, "E111.8.0.10", {"position": v(85.3, 20.32) * mm});
            skPoint(sketch, "E111.8.0.11", {"position": v(85.3, -20.32) * mm});
            skPoint(sketch, "E111.8.0.12", {"position": v(85.3, 33.98) * mm});
            skPoint(sketch, "E111.8.0.13", {"position": v(96.62, -3.3) * mm});
            skPoint(sketch, "E111.8.0.14", {"position": v(95.35, -11.18) * mm});
            skPoint(sketch, "E111.8.0.15", {"position": v(96.62, -12.45) * mm});
            skLineSegment(sketch, "E111.8.0.16", {"start": v(94.67, -4.57) * mm, "end": v(85.97, -4.57) * mm});
            skPoint(sketch, "E111.8.0.17", {"position": v(101.6, -43.18) * mm});
            skPoint(sketch, "E111.8.0.18", {"position": v(96.62, -19.05) * mm});
            skPoint(sketch, "E111.8.0.19", {"position": v(101.6, 43.18) * mm});
            skPoint(sketch, "E111.8.0.20", {"position": v(96.62, -28.2) * mm});
            skPoint(sketch, "E111.8.0.21", {"position": v(85.3, 26.92) * mm});
            skPoint(sketch, "E111.8.0.22", {"position": v(89.34, 37.35) * mm});
            skPoint(sketch, "E111.8.0.23", {"position": v(86.57, -33.45) * mm});
            skLineSegment(sketch, "E111.8.0.24", {"start": v(101.6, 44.45) * mm, "end": v(90.01, 38.94) * mm});
            skPoint(sketch, "E111.8.0.25", {"position": v(95.35, -20.32) * mm});
            skPoint(sketch, "E111.8.0.26", {"position": v(86.57, -3.3) * mm});
            skPoint(sketch, "E111.8.0.27", {"position": v(95.35, -26.92) * mm});
            skLineSegment(sketch, "E111.8.0.28", {"start": v(95.94, -19.05) * mm, "end": v(87.24, -19.05) * mm});
            skLineSegment(sketch, "E111.8.0.29", {"start": v(100.3, -42.56) * mm, "end": v(90.83, -38.06) * mm});
            skPoint(sketch, "E111.8.0.30", {"position": v(85.3, -4.57) * mm});
            skPoint(sketch, "E111.8.0.31", {"position": v(86.57, -28.2) * mm});
            skLineSegment(sketch, "E111.8.0.32", {"start": v(101.6, -44.45) * mm, "end": v(90.01, -38.94) * mm});
            skLineSegment(sketch, "E111.8.0.33", {"start": v(100.3, 42.56) * mm, "end": v(90.83, 38.06) * mm});
            skPoint(sketch, "E111.8.0.34", {"position": v(95.35, -4.57) * mm});
            skPoint(sketch, "E111.8.0.35", {"position": v(88.65, -38.29) * mm});
            skLineSegment(sketch, "E111.8.0.36", {"start": v(85.97, -11.18) * mm, "end": v(94.67, -11.18) * mm});
            skPoint(sketch, "E111.8.0.37", {"position": v(86.57, -19.05) * mm});
            skPoint(sketch, "E111.8.0.38", {"position": v(95.35, 4.57) * mm});
            skPoint(sketch, "E111.8.0.39", {"position": v(95.35, 26.92) * mm});
            skPoint(sketch, "E111.8.0.40", {"position": v(95.35, 11.18) * mm});
            skLineSegment(sketch, "E111.8.0.41", {"start": v(95.94, 19.05) * mm, "end": v(87.24, 19.05) * mm});
            skPoint(sketch, "E111.8.0.42", {"position": v(101.6, 43.18) * mm});
            skPoint(sketch, "E111.8.0.43", {"position": v(101.6, -43.18) * mm});
            skPoint(sketch, "E111.8.0.44", {"position": v(85.3, 11.18) * mm});
            skPoint(sketch, "E111.8.0.45", {"position": v(85.3, 4.57) * mm});
            skLineSegment(sketch, "E111.8.0.46", {"start": v(95.94, 3.3) * mm, "end": v(87.24, 3.3) * mm});
            skLineSegment(sketch, "E111.8.0.47", {"start": v(94.67, 4.57) * mm, "end": v(85.97, 4.57) * mm});
            skPoint(sketch, "E111.8.0.48", {"position": v(95.35, 20.32) * mm});
            skPoint(sketch, "E111.8.0.49", {"position": v(86.57, 19.05) * mm});
            skPoint(sketch, "E111.8.0.50", {"position": v(86.57, 28.2) * mm});
            skPoint(sketch, "E111.8.0.51", {"position": v(86.57, 3.3) * mm});
            skLineSegment(sketch, "E111.8.0.52", {"start": v(94.67, 20.32) * mm, "end": v(85.97, 20.32) * mm});
            skLineSegment(sketch, "E111.8.0.53", {"start": v(86.57, 12.45) * mm, "end": v(95.94, 12.45) * mm});
            skPoint(sketch, "E111.8.0.54", {"position": v(96.62, 28.2) * mm});
            skLineSegment(sketch, "E111.8.0.55", {"start": v(85.97, 11.18) * mm, "end": v(94.67, 11.18) * mm});
            skPoint(sketch, "E111.8.0.56", {"position": v(96.62, 12.45) * mm});
            skPoint(sketch, "E111.8.0.57", {"position": v(96.62, 3.3) * mm});
            skLineSegment(sketch, "E111.8.0.58", {"start": v(105.4, -43.18) * mm, "end": v(103.03, -43.18) * mm});
            skLineSegment(sketch, "E111.8.0.59", {"start": v(101.6, -44.45) * mm, "end": v(105.4, -44.45) * mm});
            skLineSegment(sketch, "E111.8.0.60", {"start": v(85.97, -26.92) * mm, "end": v(94.67, -26.92) * mm});
            skLineSegment(sketch, "E111.8.0.61", {"start": v(105.4, 43.18) * mm, "end": v(103.03, 43.18) * mm});
            skLineSegment(sketch, "E111.8.0.62", {"start": v(105.4, 44.45) * mm, "end": v(105.4, 43.18) * mm});
            skLineSegment(sketch, "E111.8.0.63", {"start": v(96.62, -27.52) * mm, "end": v(96.62, -19.72) * mm});
            skArc(sketch, "E111.8.0.64", {"start": v(90.83, 38.06) * mm, "mid": v(89.47, 37.19) * mm, "end": v(88.38, 36) * mm});
            skLineSegment(sketch, "E111.8.0.65", {"start": v(105.4, -44.45) * mm, "end": v(105.4, -43.18) * mm});
            skLineSegment(sketch, "E111.8.0.66", {"start": v(95.35, -10.5) * mm, "end": v(95.35, -5.24) * mm});
            skArc(sketch, "E111.8.0.67", {"start": v(90.01, -38.94) * mm, "mid": v(88.76, -38.15) * mm, "end": v(87.72, -37.1) * mm});
            skLineSegment(sketch, "E111.8.0.68", {"start": v(85.3, -19.65) * mm, "end": v(85.3, -11.85) * mm});
            skLineSegment(sketch, "E111.8.0.69", {"start": v(89.11, -28.2) * mm, "end": v(95.94, -28.2) * mm});
            skLineSegment(sketch, "E111.8.0.70", {"start": v(95.35, -26.25) * mm, "end": v(95.35, -21) * mm});
            skLineSegment(sketch, "E111.8.0.71", {"start": v(89.11, 28.2) * mm, "end": v(95.94, 28.2) * mm});
            skLineSegment(sketch, "E111.8.0.72", {"start": v(96.62, -11.77) * mm, "end": v(96.62, -3.97) * mm});
            skLineSegment(sketch, "E111.8.0.73", {"start": v(101.6, 44.45) * mm, "end": v(105.4, 44.45) * mm});
            skLineSegment(sketch, "E111.8.0.74", {"start": v(86.57, -18.38) * mm, "end": v(86.57, -12.45) * mm});
            skArc(sketch, "E111.8.0.75", {"start": v(90.83, -38.06) * mm, "mid": v(89.47, -37.19) * mm, "end": v(88.38, -36) * mm});
            skLineSegment(sketch, "E111.8.0.76", {"start": v(85.97, 26.92) * mm, "end": v(94.67, 26.92) * mm});
            skArc(sketch, "E111.8.0.77", {"start": v(86.64, 35.7) * mm, "mid": v(85.64, 33.86) * mm, "end": v(85.3, 31.8) * mm});
            skArc(sketch, "E111.8.0.78", {"start": v(96.62, -27.52) * mm, "mid": v(96.42, -28) * mm, "end": v(95.94, -28.2) * mm});
            skLineSegment(sketch, "E111.8.0.79", {"start": v(96.62, 27.52) * mm, "end": v(96.62, 19.72) * mm});
            skArc(sketch, "E111.8.0.80", {"start": v(94.67, -4.57) * mm, "mid": v(95.15, -4.77) * mm, "end": v(95.35, -5.24) * mm});
            skArc(sketch, "E111.8.0.81", {"start": v(86.64, -35.7) * mm, "mid": v(85.64, -33.86) * mm, "end": v(85.3, -31.8) * mm});
            skArc(sketch, "E111.8.0.82", {"start": v(85.97, -20.32) * mm, "mid": v(85.5, -20.12) * mm, "end": v(85.3, -19.65) * mm});
            skArc(sketch, "E111.8.0.83", {"start": v(95.94, -3.3) * mm, "mid": v(96.42, -3.5) * mm, "end": v(96.62, -3.97) * mm});
            skArc(sketch, "E111.8.0.84", {"start": v(87.75, 35.1) * mm, "mid": v(86.87, 33.36) * mm, "end": v(86.57, 31.43) * mm});
            skLineSegment(sketch, "E111.8.0.85", {"start": v(86.57, 18.38) * mm, "end": v(86.57, 12.45) * mm});
            skArc(sketch, "E111.8.0.86", {"start": v(87.75, -35.1) * mm, "mid": v(86.87, -33.36) * mm, "end": v(86.57, -31.43) * mm});
            skArc(sketch, "E111.8.0.87", {"start": v(86.57, -30.73) * mm, "mid": v(87.31, -28.94) * mm, "end": v(89.11, -28.2) * mm});
            skArc(sketch, "E111.8.0.88", {"start": v(95.35, -10.5) * mm, "mid": v(95.15, -10.98) * mm, "end": v(94.67, -11.18) * mm});
            skArc(sketch, "E111.8.0.89", {"start": v(85.97, 20.32) * mm, "mid": v(85.5, 20.12) * mm, "end": v(85.3, 19.65) * mm});
            skArc(sketch, "E111.8.0.90", {"start": v(90.01, 38.94) * mm, "mid": v(88.76, 38.15) * mm, "end": v(87.72, 37.1) * mm});
            skLineSegment(sketch, "E111.8.0.91", {"start": v(95.35, 10.5) * mm, "end": v(95.35, 5.24) * mm});
            skArc(sketch, "E111.8.0.92", {"start": v(86.57, 30.73) * mm, "mid": v(87.31, 28.94) * mm, "end": v(89.11, 28.2) * mm});
            skArc(sketch, "E111.8.0.93", {"start": v(103.03, 43.18) * mm, "mid": v(101.64, 43.02) * mm, "end": v(100.3, 42.56) * mm});
            skLineSegment(sketch, "E111.8.0.94", {"start": v(88.38, -36) * mm, "end": v(87.75, -35.1) * mm});
            skArc(sketch, "E111.8.0.95", {"start": v(87.24, -19.05) * mm, "mid": v(86.77, -18.85) * mm, "end": v(86.57, -18.38) * mm});
            skArc(sketch, "E111.8.0.96", {"start": v(87.24, 19.05) * mm, "mid": v(86.77, 18.85) * mm, "end": v(86.57, 18.38) * mm});
            skLineSegment(sketch, "E111.8.0.97", {"start": v(85.3, -31.8) * mm, "end": v(85.3, -27.6) * mm});
            skArc(sketch, "E111.8.0.98", {"start": v(96.62, -11.77) * mm, "mid": v(96.42, -12.25) * mm, "end": v(95.94, -12.45) * mm});
            skLineSegment(sketch, "E111.8.0.99", {"start": v(96.62, 11.77) * mm, "end": v(96.62, 3.97) * mm});
            skLineSegment(sketch, "E111.8.0.100", {"start": v(86.57, 31.43) * mm, "end": v(86.57, 30.73) * mm});
            skLineSegment(sketch, "E111.8.0.101", {"start": v(95.35, 26.25) * mm, "end": v(95.35, 21) * mm});
            skArc(sketch, "E111.8.0.102", {"start": v(94.67, -20.32) * mm, "mid": v(95.15, -20.52) * mm, "end": v(95.35, -21) * mm});
            skArc(sketch, "E111.8.0.103", {"start": v(85.3, -11.85) * mm, "mid": v(85.5, -11.37) * mm, "end": v(85.97, -11.18) * mm});
            skLineSegment(sketch, "E111.8.0.104", {"start": v(87.72, 37.1) * mm, "end": v(86.64, 35.7) * mm});
            skLineSegment(sketch, "E111.8.0.105", {"start": v(85.3, 31.8) * mm, "end": v(85.3, 27.6) * mm});
            skArc(sketch, "E111.8.0.106", {"start": v(103.03, -43.18) * mm, "mid": v(101.64, -43.02) * mm, "end": v(100.3, -42.56) * mm});
            skArc(sketch, "E111.8.0.107", {"start": v(95.94, -19.05) * mm, "mid": v(96.42, -19.25) * mm, "end": v(96.62, -19.72) * mm});
            skLineSegment(sketch, "E111.8.0.108", {"start": v(87.72, -37.1) * mm, "end": v(86.64, -35.7) * mm});
            skLineSegment(sketch, "E111.8.0.109", {"start": v(88.38, 36) * mm, "end": v(87.75, 35.1) * mm});
            skLineSegment(sketch, "E111.8.0.110", {"start": v(85.3, 19.65) * mm, "end": v(85.3, 11.85) * mm});
            skArc(sketch, "E111.8.0.111", {"start": v(95.35, -26.25) * mm, "mid": v(95.15, -26.73) * mm, "end": v(94.67, -26.92) * mm});
            skArc(sketch, "E111.8.0.112", {"start": v(85.3, -27.6) * mm, "mid": v(85.5, -27.12) * mm, "end": v(85.97, -26.92) * mm});
            skArc(sketch, "E111.8.0.113", {"start": v(94.67, 20.32) * mm, "mid": v(95.15, 20.52) * mm, "end": v(95.35, 21) * mm});
            skLineSegment(sketch, "E111.8.0.114", {"start": v(86.57, -2.63) * mm, "end": v(86.57, 0) * mm});
            skArc(sketch, "E111.8.0.115", {"start": v(87.24, 3.3) * mm, "mid": v(86.77, 3.1) * mm, "end": v(86.57, 2.63) * mm});
            skArc(sketch, "E111.8.0.116", {"start": v(95.94, 19.05) * mm, "mid": v(96.42, 19.25) * mm, "end": v(96.62, 19.72) * mm});
            skArc(sketch, "E111.8.0.117", {"start": v(94.67, 4.57) * mm, "mid": v(95.15, 4.77) * mm, "end": v(95.35, 5.24) * mm});
            skArc(sketch, "E111.8.0.118", {"start": v(95.94, 3.3) * mm, "mid": v(96.42, 3.5) * mm, "end": v(96.62, 3.97) * mm});
            skArc(sketch, "E111.8.0.119", {"start": v(96.62, 11.77) * mm, "mid": v(96.42, 12.25) * mm, "end": v(95.94, 12.45) * mm});
            skLineSegment(sketch, "E111.8.0.120", {"start": v(86.57, -31.43) * mm, "end": v(86.57, -30.73) * mm});
            skLineSegment(sketch, "E111.8.0.121", {"start": v(85.3, -3.9) * mm, "end": v(85.3, 0) * mm});
            skArc(sketch, "E111.8.0.122", {"start": v(96.62, 27.52) * mm, "mid": v(96.42, 28) * mm, "end": v(95.94, 28.2) * mm});
            skArc(sketch, "E111.8.0.123", {"start": v(95.35, 26.25) * mm, "mid": v(95.15, 26.73) * mm, "end": v(94.67, 26.92) * mm});
            skArc(sketch, "E111.8.0.124", {"start": v(85.97, -4.57) * mm, "mid": v(85.5, -4.38) * mm, "end": v(85.3, -3.9) * mm});
            skArc(sketch, "E111.8.0.125", {"start": v(87.24, -3.3) * mm, "mid": v(86.77, -3.1) * mm, "end": v(86.57, -2.63) * mm});
            skArc(sketch, "E111.8.0.126", {"start": v(85.3, 11.85) * mm, "mid": v(85.5, 11.37) * mm, "end": v(85.97, 11.18) * mm});
            skArc(sketch, "E111.8.0.127", {"start": v(85.97, 4.57) * mm, "mid": v(85.5, 4.38) * mm, "end": v(85.3, 3.9) * mm});
            skArc(sketch, "E111.8.0.128", {"start": v(85.3, 27.6) * mm, "mid": v(85.5, 27.12) * mm, "end": v(85.97, 26.92) * mm});
            skLineSegment(sketch, "E111.8.0.129", {"start": v(86.57, 2.63) * mm, "end": v(86.57, 0) * mm});
            skArc(sketch, "E111.8.0.130", {"start": v(95.35, 10.5) * mm, "mid": v(95.15, 10.98) * mm, "end": v(94.67, 11.18) * mm});
            skLineSegment(sketch, "E111.8.0.131", {"start": v(85.3, 3.9) * mm, "end": v(85.3, 0) * mm});
            skPoint(sketch, "E111.9.0.0", {"position": v(99.27, 33.45) * mm});
            skPoint(sketch, "E111.9.0.1", {"position": v(109.32, 19.05) * mm});
            skPoint(sketch, "E111.9.0.2", {"position": v(98, -26.92) * mm});
            skLineSegment(sketch, "E111.9.0.3", {"start": v(99.27, -12.45) * mm, "end": v(108.64, -12.45) * mm});
            skLineSegment(sketch, "E111.9.0.4", {"start": v(107.37, -20.32) * mm, "end": v(98.67, -20.32) * mm});
            skPoint(sketch, "E111.9.0.5", {"position": v(98, -33.98) * mm});
            skPoint(sketch, "E111.9.0.6", {"position": v(101.35, 38.29) * mm});
            skPoint(sketch, "E111.9.0.7", {"position": v(102.04, -37.35) * mm});
            skPoint(sketch, "E111.9.0.8", {"position": v(98, -11.18) * mm});
            skLineSegment(sketch, "E111.9.0.9", {"start": v(108.64, -3.3) * mm, "end": v(99.94, -3.3) * mm});
            skPoint(sketch, "E111.9.0.10", {"position": v(98, 20.32) * mm});
            skPoint(sketch, "E111.9.0.11", {"position": v(98, -20.32) * mm});
            skPoint(sketch, "E111.9.0.12", {"position": v(98, 33.98) * mm});
            skPoint(sketch, "E111.9.0.13", {"position": v(109.32, -3.3) * mm});
            skPoint(sketch, "E111.9.0.14", {"position": v(108.05, -11.18) * mm});
            skPoint(sketch, "E111.9.0.15", {"position": v(109.32, -12.45) * mm});
            skLineSegment(sketch, "E111.9.0.16", {"start": v(107.37, -4.57) * mm, "end": v(98.67, -4.57) * mm});
            skPoint(sketch, "E111.9.0.17", {"position": v(114.3, -43.18) * mm});
            skPoint(sketch, "E111.9.0.18", {"position": v(109.32, -19.05) * mm});
            skPoint(sketch, "E111.9.0.19", {"position": v(114.3, 43.18) * mm});
            skPoint(sketch, "E111.9.0.20", {"position": v(109.32, -28.2) * mm});
            skPoint(sketch, "E111.9.0.21", {"position": v(98, 26.92) * mm});
            skPoint(sketch, "E111.9.0.22", {"position": v(102.04, 37.35) * mm});
            skPoint(sketch, "E111.9.0.23", {"position": v(99.27, -33.45) * mm});
            skLineSegment(sketch, "E111.9.0.24", {"start": v(114.3, 44.45) * mm, "end": v(102.71, 38.94) * mm});
            skPoint(sketch, "E111.9.0.25", {"position": v(108.05, -20.32) * mm});
            skPoint(sketch, "E111.9.0.26", {"position": v(99.27, -3.3) * mm});
            skPoint(sketch, "E111.9.0.27", {"position": v(108.05, -26.92) * mm});
            skLineSegment(sketch, "E111.9.0.28", {"start": v(108.64, -19.05) * mm, "end": v(99.94, -19.05) * mm});
            skLineSegment(sketch, "E111.9.0.29", {"start": v(113, -42.56) * mm, "end": v(103.53, -38.06) * mm});
            skPoint(sketch, "E111.9.0.30", {"position": v(98, -4.57) * mm});
            skPoint(sketch, "E111.9.0.31", {"position": v(99.27, -28.2) * mm});
            skLineSegment(sketch, "E111.9.0.32", {"start": v(114.3, -44.45) * mm, "end": v(102.71, -38.94) * mm});
            skLineSegment(sketch, "E111.9.0.33", {"start": v(113, 42.56) * mm, "end": v(103.53, 38.06) * mm});
            skPoint(sketch, "E111.9.0.34", {"position": v(108.05, -4.57) * mm});
            skPoint(sketch, "E111.9.0.35", {"position": v(101.35, -38.29) * mm});
            skLineSegment(sketch, "E111.9.0.36", {"start": v(98.67, -11.18) * mm, "end": v(107.37, -11.18) * mm});
            skPoint(sketch, "E111.9.0.37", {"position": v(99.27, -19.05) * mm});
            skPoint(sketch, "E111.9.0.38", {"position": v(108.05, 4.57) * mm});
            skPoint(sketch, "E111.9.0.39", {"position": v(108.05, 26.92) * mm});
            skPoint(sketch, "E111.9.0.40", {"position": v(108.05, 11.18) * mm});
            skLineSegment(sketch, "E111.9.0.41", {"start": v(108.64, 19.05) * mm, "end": v(99.94, 19.05) * mm});
            skPoint(sketch, "E111.9.0.42", {"position": v(114.3, 43.18) * mm});
            skPoint(sketch, "E111.9.0.43", {"position": v(114.3, -43.18) * mm});
            skPoint(sketch, "E111.9.0.44", {"position": v(98, 11.18) * mm});
            skPoint(sketch, "E111.9.0.45", {"position": v(98, 4.57) * mm});
            skLineSegment(sketch, "E111.9.0.46", {"start": v(108.64, 3.3) * mm, "end": v(99.94, 3.3) * mm});
            skLineSegment(sketch, "E111.9.0.47", {"start": v(107.37, 4.57) * mm, "end": v(98.67, 4.57) * mm});
            skPoint(sketch, "E111.9.0.48", {"position": v(108.05, 20.32) * mm});
            skPoint(sketch, "E111.9.0.49", {"position": v(99.27, 19.05) * mm});
            skPoint(sketch, "E111.9.0.50", {"position": v(99.27, 28.2) * mm});
            skPoint(sketch, "E111.9.0.51", {"position": v(99.27, 3.3) * mm});
            skLineSegment(sketch, "E111.9.0.52", {"start": v(107.37, 20.32) * mm, "end": v(98.67, 20.32) * mm});
            skLineSegment(sketch, "E111.9.0.53", {"start": v(99.27, 12.45) * mm, "end": v(108.64, 12.45) * mm});
            skPoint(sketch, "E111.9.0.54", {"position": v(109.32, 28.2) * mm});
            skLineSegment(sketch, "E111.9.0.55", {"start": v(98.67, 11.18) * mm, "end": v(107.37, 11.18) * mm});
            skPoint(sketch, "E111.9.0.56", {"position": v(109.32, 12.45) * mm});
            skPoint(sketch, "E111.9.0.57", {"position": v(109.32, 3.3) * mm});
            skLineSegment(sketch, "E111.9.0.58", {"start": v(118.11, -43.18) * mm, "end": v(115.73, -43.18) * mm});
            skLineSegment(sketch, "E111.9.0.59", {"start": v(114.3, -44.45) * mm, "end": v(118.11, -44.45) * mm});
            skLineSegment(sketch, "E111.9.0.60", {"start": v(98.67, -26.92) * mm, "end": v(107.37, -26.92) * mm});
            skLineSegment(sketch, "E111.9.0.61", {"start": v(118.11, 43.18) * mm, "end": v(115.73, 43.18) * mm});
            skLineSegment(sketch, "E111.9.0.62", {"start": v(118.11, 44.45) * mm, "end": v(118.11, 43.18) * mm});
            skLineSegment(sketch, "E111.9.0.63", {"start": v(109.32, -27.52) * mm, "end": v(109.32, -19.72) * mm});
            skArc(sketch, "E111.9.0.64", {"start": v(103.53, 38.06) * mm, "mid": v(102.17, 37.19) * mm, "end": v(101.08, 36) * mm});
            skLineSegment(sketch, "E111.9.0.65", {"start": v(118.11, -44.45) * mm, "end": v(118.11, -43.18) * mm});
            skLineSegment(sketch, "E111.9.0.66", {"start": v(108.05, -10.5) * mm, "end": v(108.05, -5.24) * mm});
            skArc(sketch, "E111.9.0.67", {"start": v(102.71, -38.94) * mm, "mid": v(101.46, -38.15) * mm, "end": v(100.42, -37.1) * mm});
            skLineSegment(sketch, "E111.9.0.68", {"start": v(98, -19.65) * mm, "end": v(98, -11.85) * mm});
            skLineSegment(sketch, "E111.9.0.69", {"start": v(101.81, -28.2) * mm, "end": v(108.64, -28.2) * mm});
            skLineSegment(sketch, "E111.9.0.70", {"start": v(108.05, -26.25) * mm, "end": v(108.05, -21) * mm});
            skLineSegment(sketch, "E111.9.0.71", {"start": v(101.81, 28.2) * mm, "end": v(108.64, 28.2) * mm});
            skLineSegment(sketch, "E111.9.0.72", {"start": v(109.32, -11.77) * mm, "end": v(109.32, -3.97) * mm});
            skLineSegment(sketch, "E111.9.0.73", {"start": v(114.3, 44.45) * mm, "end": v(118.11, 44.45) * mm});
            skLineSegment(sketch, "E111.9.0.74", {"start": v(99.27, -18.38) * mm, "end": v(99.27, -12.45) * mm});
            skArc(sketch, "E111.9.0.75", {"start": v(103.53, -38.06) * mm, "mid": v(102.17, -37.19) * mm, "end": v(101.08, -36) * mm});
            skLineSegment(sketch, "E111.9.0.76", {"start": v(98.67, 26.92) * mm, "end": v(107.37, 26.92) * mm});
            skArc(sketch, "E111.9.0.77", {"start": v(99.34, 35.7) * mm, "mid": v(98.34, 33.86) * mm, "end": v(98, 31.8) * mm});
            skArc(sketch, "E111.9.0.78", {"start": v(109.32, -27.52) * mm, "mid": v(109.12, -28) * mm, "end": v(108.64, -28.2) * mm});
            skLineSegment(sketch, "E111.9.0.79", {"start": v(109.32, 27.52) * mm, "end": v(109.32, 19.72) * mm});
            skArc(sketch, "E111.9.0.80", {"start": v(107.37, -4.57) * mm, "mid": v(107.85, -4.77) * mm, "end": v(108.05, -5.24) * mm});
            skArc(sketch, "E111.9.0.81", {"start": v(99.34, -35.7) * mm, "mid": v(98.34, -33.86) * mm, "end": v(98, -31.8) * mm});
            skArc(sketch, "E111.9.0.82", {"start": v(98.67, -20.32) * mm, "mid": v(98.2, -20.12) * mm, "end": v(98, -19.65) * mm});
            skArc(sketch, "E111.9.0.83", {"start": v(108.64, -3.3) * mm, "mid": v(109.12, -3.5) * mm, "end": v(109.32, -3.97) * mm});
            skArc(sketch, "E111.9.0.84", {"start": v(100.45, 35.1) * mm, "mid": v(99.57, 33.36) * mm, "end": v(99.27, 31.43) * mm});
            skLineSegment(sketch, "E111.9.0.85", {"start": v(99.27, 18.38) * mm, "end": v(99.27, 12.45) * mm});
            skArc(sketch, "E111.9.0.86", {"start": v(100.45, -35.1) * mm, "mid": v(99.57, -33.36) * mm, "end": v(99.27, -31.43) * mm});
            skArc(sketch, "E111.9.0.87", {"start": v(99.27, -30.73) * mm, "mid": v(100.01, -28.94) * mm, "end": v(101.81, -28.2) * mm});
            skArc(sketch, "E111.9.0.88", {"start": v(108.05, -10.5) * mm, "mid": v(107.85, -10.98) * mm, "end": v(107.37, -11.18) * mm});
            skArc(sketch, "E111.9.0.89", {"start": v(98.67, 20.32) * mm, "mid": v(98.2, 20.12) * mm, "end": v(98, 19.65) * mm});
            skArc(sketch, "E111.9.0.90", {"start": v(102.71, 38.94) * mm, "mid": v(101.46, 38.15) * mm, "end": v(100.42, 37.1) * mm});
            skLineSegment(sketch, "E111.9.0.91", {"start": v(108.05, 10.5) * mm, "end": v(108.05, 5.24) * mm});
            skArc(sketch, "E111.9.0.92", {"start": v(99.27, 30.73) * mm, "mid": v(100.01, 28.94) * mm, "end": v(101.81, 28.2) * mm});
            skArc(sketch, "E111.9.0.93", {"start": v(115.73, 43.18) * mm, "mid": v(114.34, 43.02) * mm, "end": v(113, 42.56) * mm});
            skLineSegment(sketch, "E111.9.0.94", {"start": v(101.08, -36) * mm, "end": v(100.45, -35.1) * mm});
            skArc(sketch, "E111.9.0.95", {"start": v(99.94, -19.05) * mm, "mid": v(99.47, -18.85) * mm, "end": v(99.27, -18.38) * mm});
            skArc(sketch, "E111.9.0.96", {"start": v(99.94, 19.05) * mm, "mid": v(99.47, 18.85) * mm, "end": v(99.27, 18.38) * mm});
            skLineSegment(sketch, "E111.9.0.97", {"start": v(98, -31.8) * mm, "end": v(98, -27.6) * mm});
            skArc(sketch, "E111.9.0.98", {"start": v(109.32, -11.77) * mm, "mid": v(109.12, -12.25) * mm, "end": v(108.64, -12.45) * mm});
            skLineSegment(sketch, "E111.9.0.99", {"start": v(109.32, 11.77) * mm, "end": v(109.32, 3.97) * mm});
            skLineSegment(sketch, "E111.9.0.100", {"start": v(99.27, 31.43) * mm, "end": v(99.27, 30.73) * mm});
            skLineSegment(sketch, "E111.9.0.101", {"start": v(108.05, 26.25) * mm, "end": v(108.05, 21) * mm});
            skArc(sketch, "E111.9.0.102", {"start": v(107.37, -20.32) * mm, "mid": v(107.85, -20.52) * mm, "end": v(108.05, -21) * mm});
            skArc(sketch, "E111.9.0.103", {"start": v(98, -11.85) * mm, "mid": v(98.2, -11.37) * mm, "end": v(98.67, -11.18) * mm});
            skLineSegment(sketch, "E111.9.0.104", {"start": v(100.42, 37.1) * mm, "end": v(99.34, 35.7) * mm});
            skLineSegment(sketch, "E111.9.0.105", {"start": v(98, 31.8) * mm, "end": v(98, 27.6) * mm});
            skArc(sketch, "E111.9.0.106", {"start": v(115.73, -43.18) * mm, "mid": v(114.34, -43.02) * mm, "end": v(113, -42.56) * mm});
            skArc(sketch, "E111.9.0.107", {"start": v(108.64, -19.05) * mm, "mid": v(109.12, -19.25) * mm, "end": v(109.32, -19.72) * mm});
            skLineSegment(sketch, "E111.9.0.108", {"start": v(100.42, -37.1) * mm, "end": v(99.34, -35.7) * mm});
            skLineSegment(sketch, "E111.9.0.109", {"start": v(101.08, 36) * mm, "end": v(100.45, 35.1) * mm});
            skLineSegment(sketch, "E111.9.0.110", {"start": v(98, 19.65) * mm, "end": v(98, 11.85) * mm});
            skArc(sketch, "E111.9.0.111", {"start": v(108.05, -26.25) * mm, "mid": v(107.85, -26.73) * mm, "end": v(107.37, -26.92) * mm});
            skArc(sketch, "E111.9.0.112", {"start": v(98, -27.6) * mm, "mid": v(98.2, -27.12) * mm, "end": v(98.67, -26.92) * mm});
            skArc(sketch, "E111.9.0.113", {"start": v(107.37, 20.32) * mm, "mid": v(107.85, 20.52) * mm, "end": v(108.05, 21) * mm});
            skLineSegment(sketch, "E111.9.0.114", {"start": v(99.27, -2.63) * mm, "end": v(99.27, 0) * mm});
            skArc(sketch, "E111.9.0.115", {"start": v(99.94, 3.3) * mm, "mid": v(99.47, 3.1) * mm, "end": v(99.27, 2.63) * mm});
            skArc(sketch, "E111.9.0.116", {"start": v(108.64, 19.05) * mm, "mid": v(109.12, 19.25) * mm, "end": v(109.32, 19.72) * mm});
            skArc(sketch, "E111.9.0.117", {"start": v(107.37, 4.57) * mm, "mid": v(107.85, 4.77) * mm, "end": v(108.05, 5.24) * mm});
            skArc(sketch, "E111.9.0.118", {"start": v(108.64, 3.3) * mm, "mid": v(109.12, 3.5) * mm, "end": v(109.32, 3.97) * mm});
            skArc(sketch, "E111.9.0.119", {"start": v(109.32, 11.77) * mm, "mid": v(109.12, 12.25) * mm, "end": v(108.64, 12.45) * mm});
            skLineSegment(sketch, "E111.9.0.120", {"start": v(99.27, -31.43) * mm, "end": v(99.27, -30.73) * mm});
            skLineSegment(sketch, "E111.9.0.121", {"start": v(98, -3.9) * mm, "end": v(98, 0) * mm});
            skArc(sketch, "E111.9.0.122", {"start": v(109.32, 27.52) * mm, "mid": v(109.12, 28) * mm, "end": v(108.64, 28.2) * mm});
            skArc(sketch, "E111.9.0.123", {"start": v(108.05, 26.25) * mm, "mid": v(107.85, 26.73) * mm, "end": v(107.37, 26.92) * mm});
            skArc(sketch, "E111.9.0.124", {"start": v(98.67, -4.57) * mm, "mid": v(98.2, -4.38) * mm, "end": v(98, -3.9) * mm});
            skArc(sketch, "E111.9.0.125", {"start": v(99.94, -3.3) * mm, "mid": v(99.47, -3.1) * mm, "end": v(99.27, -2.63) * mm});
            skArc(sketch, "E111.9.0.126", {"start": v(98, 11.85) * mm, "mid": v(98.2, 11.37) * mm, "end": v(98.67, 11.18) * mm});
            skArc(sketch, "E111.9.0.127", {"start": v(98.67, 4.57) * mm, "mid": v(98.2, 4.38) * mm, "end": v(98, 3.9) * mm});
            skArc(sketch, "E111.9.0.128", {"start": v(98, 27.6) * mm, "mid": v(98.2, 27.12) * mm, "end": v(98.67, 26.92) * mm});
            skLineSegment(sketch, "E111.9.0.129", {"start": v(99.27, 2.63) * mm, "end": v(99.27, 0) * mm});
            skArc(sketch, "E111.9.0.130", {"start": v(108.05, 10.5) * mm, "mid": v(107.85, 10.98) * mm, "end": v(107.37, 11.18) * mm});
            skLineSegment(sketch, "E111.9.0.131", {"start": v(98, 3.9) * mm, "end": v(98, 0) * mm});
            skLineSegment(sketch, "E111.direction1", {"start": v(-12.95, -38.29) * mm, "end": v(-0.25, -38.29) * mm, "construction": true});
            skSolve(sketch);
        }
        {
            var Q0;
            Q0 = qSketchRegion(id + "F0", true);
            extrude(context, id + "F1", {"entities" : qUnion([Q0]), "depth" : 2.54 * mm, "offsetDistance" : 25.4 * mm});
        }
    });
